FREECAD ASSEMBLY — COMPONENT RECIPES ("tripod_base")

This assembly document has 14 components, labeled P0..P13 below (a component is one placed body or linked part). 14 of them carry a construction recipe — the FreeCAD feature program that regenerates the part from scratch, quoted from this document or its linked companion documents; the rest are supplied as boundary geometry only. No exploded tour is included for this assembly.
NOTE — document 2 of 2 of this assembly tour. The two overview renders and the header above are repeated from document 1; the component sections below continue where the previous document stopped.
COMPONENT P9 — recipe-attached ("Plate", modeled in this document).
Construction recipe (the document's own serialized feature program — sketch geometry with constraints, then the solid features built on it; lengths are millimeters unless a unit is written):

FEATURE [PartDesign::SubShapeBinder] Binder
  BindCopyOnChange = 0
  BindMode = 0
  ClaimChildren = false
  Context = -> Part012 [Body017.Binder.]
  Fuse = false
  MakeFace = true
  OffsetFill = false
  OffsetIntersection = false
  OffsetJoinType = 0
  OffsetOpenResult = false
  PartialLoad = false
  Relative = true
  Support = -> [Part005[Body007.]]
  _Version = 2
FEATURE [Sketcher::SketchObject] Sketch060
  ArcFitTolerance = 1e-06
  AttachmentSupport = -> [Binder]
  ExternalGeometry = -> [Binder]
  FullyConstrained = false
  MakeInternals = false
  MapMode = 5
  Placement = pos=(0,0,11) rot=(1,0,0;3.14159rad)
  sketch-geometry (30):
    g0: LineSegment [constr] StartX=-65.0269 StartY=11.2868 StartZ=0 EndX=-11.2868 EndY=65.0269 EndZ=0
    g1: LineSegment [constr] StartX=-11.2868 StartY=65.0269 StartZ=0 EndX=27.9576 EndY=25.7825 EndZ=0
    g2: LineSegment [constr] StartX=27.9576 StartY=25.7825 StartZ=0 EndX=-25.7825 EndY=-27.9576 EndZ=0
    g3: LineSegment [constr] StartX=-25.7825 StartY=-27.9576 StartZ=0 EndX=-65.0269 EndY=11.2868 EndZ=0
    g4: LineSegment [constr] StartX=-38.1569 StartY=38.1569 StartZ=0 EndX=1.08757 EndY=-1.08757 EndZ=0
    g5: Circle CenterX=-65.0269 CenterY=11.2868 CenterZ=0 NormalX=0 NormalY=0 NormalZ=1 AngleXU=0 Radius=1.25
    g6: Circle CenterX=-25.7825 CenterY=-27.9576 CenterZ=0 NormalX=0 NormalY=0 NormalZ=1 AngleXU=0 Radius=1.25
    g7: Circle CenterX=27.9576 CenterY=25.7825 CenterZ=0 NormalX=0 NormalY=0 NormalZ=1 AngleXU=0 Radius=1.25
    g8: Circle CenterX=-11.2868 CenterY=65.0269 CenterZ=0 NormalX=0 NormalY=0 NormalZ=1 AngleXU=0 Radius=1.25
    g9: Circle CenterX=-36.7426 CenterY=39.5711 CenterZ=0 NormalX=0 NormalY=0 NormalZ=1 AngleXU=0 Radius=1.25
    g10: Circle CenterX=-39.5711 CenterY=36.7426 CenterZ=0 NormalX=0 NormalY=0 NormalZ=1 AngleXU=0 Radius=1.25
    g11: Circle CenterX=-0.326641 CenterY=-2.50179 CenterZ=0 NormalX=0 NormalY=0 NormalZ=1 AngleXU=0 Radius=1.25
    g12: Circle CenterX=2.50179 CenterY=0.326641 CenterZ=0 NormalX=0 NormalY=0 NormalZ=1 AngleXU=0 Radius=1.25
    g13: GeomPoint [constr] X=-18.5346 Y=18.5346 Z=0
    g14: LineSegment [constr] StartX=0 StartY=65 StartZ=0 EndX=-65 EndY=0 EndZ=0
    g15: GeomPoint [constr] X=-32.5 Y=32.5 Z=0
    g16: LineSegment StartX=-68.5624 StartY=14.8223 StartZ=0 EndX=-14.8223 EndY=68.5624 EndZ=0
    g17: LineSegment StartX=30.079 StartY=23.6612 StartZ=0 EndX=-23.6612 EndY=-30.079 EndZ=0
    g18: ArcOfCircle CenterX=-11.2868 CenterY=65.0269 CenterZ=0 NormalX=0 NormalY=0 NormalZ=1 AngleXU=0 Radius=5 StartAngle=1.56841 EndAngle=2.35619
    g19: ArcOfCircle CenterX=0 CenterY=65 CenterZ=0 NormalX=0 NormalY=0 NormalZ=1 AngleXU=0 Radius=5 StartAngle=0.577784 EndAngle=1.56841
    g20: LineSegment StartX=-11.2749 StartY=70.0269 StartZ=0 EndX=0.0119218 EndY=70 EndZ=0
    g21: ArcOfCircle CenterX=27.9576 CenterY=25.7825 CenterZ=0 NormalX=0 NormalY=0 NormalZ=1 AngleXU=0 Radius=3 StartAngle=5.49779 EndAngle=6.86097
    g22: LineSegment StartX=4.18837 StartY=67.7308 StartZ=0 EndX=30.4707 EndY=27.421 EndZ=0
    g23: ArcOfCircle CenterX=-25.7825 CenterY=-27.9576 CenterZ=0 NormalX=0 NormalY=0 NormalZ=1 AngleXU=0 Radius=3 StartAngle=4.1346 EndAngle=5.49779
    g24: ArcOfCircle CenterX=-65.0269 CenterY=11.2868 CenterZ=0 NormalX=0 NormalY=0 NormalZ=1 AngleXU=0 Radius=5 StartAngle=2.35619 EndAngle=3.14398
    g25: ArcOfCircle CenterX=-65 CenterY=0 CenterZ=0 NormalX=0 NormalY=0 NormalZ=1 AngleXU=0 Radius=5 StartAngle=3.14398 EndAngle=4.1346
    g26: LineSegment StartX=-70.0269 StartY=11.2749 StartZ=0 EndX=-70 EndY=-0.0119218 EndZ=0
    g27: LineSegment StartX=-67.7308 StartY=-4.18837 StartZ=0 EndX=-27.421 EndY=-30.4707 EndZ=0
    g28: Circle CenterX=0 CenterY=65 CenterZ=0 NormalX=0 NormalY=0 NormalZ=1 AngleXU=0 Radius=1.65
    g29: Circle CenterX=-65 CenterY=0 CenterZ=0 NormalX=0 NormalY=0 NormalZ=1 AngleXU=0 Radius=1.65
  constraints (74):
    c: Coincident(g0,g1)
    c: Coincident(g1,g2)
    c: Coincident(g2,g3)
    c: Coincident(g3,g0)
    c: Angle(g3,g0) = 1.5708
    c: Angle(g0,g1) = 1.5708
    c: Equal(g1,g3)
    c: Symmetric(g0,g0,g4)
    c: Symmetric(g2,g2,g4)
    c: Distance(g0,g0) = 76
    c: Coincident(g5,g0)
    c: Coincident(g6,g2)
    c: Coincident(g7,g1)
    c: Coincident(g8,g0)
    c: PointOnObject(g9,g0)
    c: PointOnObject(g11,g2)
    c: Symmetric(g9,g10,g4)
    c: Symmetric(g12,g11,g4)
    c: Equal(g8,g9)
    c: Equal(g10,g5)
    c: Equal(g6,g11)
    c: Equal(g12,g7)
    c: Equal(g7,g8)
    c: Equal(g6,g5)
    c: Equal(g8,g5)
    c: Diameter(g8) = 2.5
    c: Distance(g10,g9) = 4
    c: Distance(g12,g11) = 4
    c: Distance(g1,g1) = 55.5
    c: Symmetric(g4,g4,g13)
    c: Parallel(g0,g14)
    c: Symmetric(g14,g14,g15)
    c: PointOnObject(g15,g4)
    c: Coincident(g14,g-4)
    c: Coincident(g14,g-3)
    c: Distance(g15,g4) = 8
    c: Coincident(g18,g0)
    c: Coincident(g18,g16)
    c: Angle(g16,g18,g16) = 3.14159
    c: Coincident(g19,g14)
    c: Coincident(g20,g18)
    c: Coincident(g20,g19)
    c: Angle(g20,g18,g18) = 3.14159
    c: Angle(g19,g20,g19) = 3.14159
    c: Radius(g19) = 5
    c: Radius(g18) = 5
    c: Coincident(g21,g1)
    c: Coincident(g17,g21)
    c: Angle(g17,g21,g17) = 3.14159
    c: Coincident(g22,g19)
    c: Coincident(g22,g21)
    c: Angle(g21,g22,g21) = 3.14159
    c: Radius(g21) = 3
    c: Coincident(g23,g2)
    c: Coincident(g17,g23)
    c: Angle(g17,g23,g17) = 3.14159
    c: Coincident(g24,g0)
    c: Coincident(g25,g14)
    c: Coincident(g16,g24)
    c: Angle(g16,g24,g16) = 3.14159
    c: Coincident(g26,g24)
    c: Coincident(g26,g25)
    c: Angle(g25,g26,g25) = 0
    c: Equal(g24,g25)
    c: Equal(g24,g18)
    c: Angle(g26,g24,g24) = 0
    c: Coincident(g27,g25)
    c: Coincident(g27,g23)
    c: Angle(g23,g27,g23) = 0
    c: Angle(g27,g25,g25) = 0
    c: Equal(g21,g23)
    c: Angle(g22,g19,g19) = 3.14159
    c: Coincident(g28,g14)
    c: Coincident(g29,g14)
FEATURE [PartDesign::Pad] Pad017
  Direction = (0,0,-1)
  Length = 5
  Length2 = 10
  Profile = -> Sketch060
  ReferenceAxis = -> Sketch060 [N_Axis]
  Suppressed = false
  Type = 0
FEATURE [Sketcher::SketchObject] Sketch061
  ArcFitTolerance = 1e-06
  AttachmentSupport = -> [Pad017]
  ExternalGeometry = -> [Pad017]
  FullyConstrained = false
  MakeInternals = false
  MapMode = 5
  Placement = pos=(0,0,11) rot=(0,0,1;0rad)
  sketch-geometry (4):
    g0: Circle CenterX=-65 CenterY=0 CenterZ=0 NormalX=0 NormalY=0 NormalZ=1 AngleXU=0 Radius=3.25
    g1: Circle CenterX=0 CenterY=-65 CenterZ=0 NormalX=0 NormalY=0 NormalZ=1 AngleXU=0 Radius=3.25
    g2: Circle CenterX=0 CenterY=-65 CenterZ=0 NormalX=0 NormalY=0 NormalZ=1 AngleXU=0 Radius=1.65
    g3: Circle CenterX=-65 CenterY=0 CenterZ=0 NormalX=0 NormalY=0 NormalZ=1 AngleXU=0 Radius=1.65
  constraints (6):
    c: Coincident(g0,g-4)
    c: Coincident(g1,g-3)
    c: Equal(g0,g1)
    c: Diameter(g1) = 6.5
    c: Coincident(g2,g1)
    c: Coincident(g3,g0)
FEATURE [PartDesign::Pad] Pad018
  BaseFeature = -> Pad017
  Direction = (0,0,1)
  Length = 2
  Length2 = 10
  Profile = -> Sketch061
  ReferenceAxis = -> Sketch061 [N_Axis]
  Suppressed = false
  Type = 0
FEATURE [PartDesign::Fillet] Fillet004
  Base = -> Pad018 [Edge23,Edge26]
  BaseFeature = -> Pad018
  Radius = 1
  SupportTransform = false
  Suppressed = false
  UseAllEdges = false
FEATURE [Sketcher::SketchObject] Sketch062
  ArcFitTolerance = 1e-06
  AttachmentSupport = -> [Fillet004]
  ExternalGeometry = -> [Fillet004]
  FullyConstrained = false
  MakeInternals = false
  MapMode = 5
  Placement = pos=(0,0,11) rot=(0,0,1;0rad)
  sketch-geometry (56):
    g0: LineSegment StartX=-63.0269 StartY=-12.4415 StartZ=0 EndX=-63.0269 EndY=-10.1321 EndZ=0
    g1: LineSegment StartX=-63.0269 StartY=-10.1321 StartZ=0 EndX=-65.0269 EndY=-8.9774 EndZ=0
    g2: LineSegment StartX=-65.0269 StartY=-8.9774 StartZ=0 EndX=-67.0269 EndY=-10.1321 EndZ=0
    g3: LineSegment StartX=-67.0269 StartY=-10.1321 StartZ=0 EndX=-67.0269 EndY=-12.4415 EndZ=0
    g4: LineSegment StartX=-67.0269 StartY=-12.4415 StartZ=0 EndX=-65.0269 EndY=-13.5962 EndZ=0
    g5: LineSegment StartX=-65.0269 StartY=-13.5962 StartZ=0 EndX=-63.0269 EndY=-12.4415 EndZ=0
    g6: Circle [constr] CenterX=-65.0269 CenterY=-11.2868 CenterZ=0 NormalX=0 NormalY=0 NormalZ=1 AngleXU=0 Radius=2.3094
    g7: LineSegment StartX=-41.8018 StartY=-36.1449 StartZ=0 EndX=-41.2041 EndY=-38.3756 EndZ=0
    g8: LineSegment StartX=-41.2041 StartY=-38.3756 StartZ=0 EndX=-38.9734 EndY=-38.9734 EndZ=0
    g9: LineSegment StartX=-38.9734 StartY=-38.9734 StartZ=0 EndX=-37.3404 EndY=-37.3404 EndZ=0
    g10: LineSegment StartX=-37.3404 StartY=-37.3404 StartZ=0 EndX=-37.9381 EndY=-35.1096 EndZ=0
    g11: LineSegment StartX=-37.9381 StartY=-35.1096 StartZ=0 EndX=-40.1688 EndY=-34.5119 EndZ=0
    g12: LineSegment StartX=-40.1688 StartY=-34.5119 StartZ=0 EndX=-41.8018 EndY=-36.1449 EndZ=0
    g13: Circle [constr] CenterX=-39.5711 CenterY=-36.7426 CenterZ=0 NormalX=0 NormalY=0 NormalZ=1 AngleXU=0 Radius=2.3094
    g14: LineSegment StartX=-35.1096 StartY=-37.9381 StartZ=0 EndX=-37.3404 EndY=-37.3404 EndZ=0
    g15: LineSegment StartX=-37.3404 StartY=-37.3404 StartZ=0 EndX=-38.9734 EndY=-38.9734 EndZ=0
    g16: LineSegment StartX=-38.9734 StartY=-38.9734 StartZ=0 EndX=-38.3756 EndY=-41.2041 EndZ=0
    g17: LineSegment StartX=-38.3756 StartY=-41.2041 StartZ=0 EndX=-36.1449 EndY=-41.8018 EndZ=0
    g18: LineSegment StartX=-36.1449 StartY=-41.8018 StartZ=0 EndX=-34.5119 EndY=-40.1688 EndZ=0
    g19: LineSegment StartX=-34.5119 StartY=-40.1688 StartZ=0 EndX=-35.1096 EndY=-37.9381 EndZ=0
    g20: Circle [constr] CenterX=-36.7426 CenterY=-39.5711 CenterZ=0 NormalX=0 NormalY=0 NormalZ=1 AngleXU=0 Radius=2.3094
    g21: LineSegment StartX=-11.2868 StartY=-62.7175 StartZ=0 EndX=-13.2868 EndY=-63.8722 EndZ=0
    g22: LineSegment StartX=-13.2868 StartY=-63.8722 StartZ=0 EndX=-13.2868 EndY=-66.1816 EndZ=0
    g23: LineSegment StartX=-13.2868 StartY=-66.1816 StartZ=0 EndX=-11.2868 EndY=-67.3363 EndZ=0
    g24: LineSegment StartX=-11.2868 StartY=-67.3363 StartZ=0 EndX=-9.2868 EndY=-66.1816 EndZ=0
    g25: LineSegment StartX=-9.2868 StartY=-66.1816 StartZ=0 EndX=-9.2868 EndY=-63.8722 EndZ=0
    g26: LineSegment StartX=-9.2868 StartY=-63.8722 StartZ=0 EndX=-11.2868 EndY=-62.7175 EndZ=0
    g27: Circle [constr] CenterX=-11.2868 CenterY=-65.0269 CenterZ=0 NormalX=0 NormalY=0 NormalZ=1 AngleXU=0 Radius=2.3094
    g28: LineSegment StartX=29.1123 StartY=-23.7825 StartZ=0 EndX=26.8029 EndY=-23.7825 EndZ=0
    g29: LineSegment StartX=26.8029 StartY=-23.7825 StartZ=0 EndX=25.6482 EndY=-25.7825 EndZ=0
    g30: LineSegment StartX=25.6482 StartY=-25.7825 StartZ=0 EndX=26.8029 EndY=-27.7825 EndZ=0
    g31: LineSegment StartX=26.8029 StartY=-27.7825 StartZ=0 EndX=29.1123 EndY=-27.7825 EndZ=0
    g32: LineSegment StartX=29.1123 StartY=-27.7825 StartZ=0 EndX=30.267 EndY=-25.7825 EndZ=0
    g33: LineSegment StartX=30.267 StartY=-25.7825 StartZ=0 EndX=29.1123 EndY=-23.7825 EndZ=0
    g34: Circle [constr] CenterX=27.9576 CenterY=-25.7825 CenterZ=0 NormalX=0 NormalY=0 NormalZ=1 AngleXU=0 Radius=2.3094
    g35: LineSegment StartX=4.7325 StartY=-0.924358 StartZ=0 EndX=4.13478 EndY=1.30635 EndZ=0
    g36: LineSegment StartX=4.13478 StartY=1.30635 StartZ=0 EndX=1.90407 EndY=1.90407 EndZ=0
    g37: LineSegment StartX=1.90407 StartY=1.90407 StartZ=0 EndX=0.271076 EndY=0.271076 EndZ=0
    g38: LineSegment StartX=0.271076 StartY=0.271076 StartZ=0 EndX=0.868793 EndY=-1.95963 EndZ=0
    g39: LineSegment StartX=0.868793 StartY=-1.95963 StartZ=0 EndX=3.0995 EndY=-2.55735 EndZ=0
    g40: LineSegment StartX=3.0995 StartY=-2.55735 StartZ=0 EndX=4.7325 EndY=-0.924358 EndZ=0
    g41: Circle [constr] CenterX=2.50179 CenterY=-0.326641 CenterZ=0 NormalX=0 NormalY=0 NormalZ=1 AngleXU=0 Radius=2.3094
    g42: LineSegment StartX=-2.55735 StartY=3.0995 StartZ=0 EndX=-1.95963 EndY=0.868793 EndZ=0
    g43: LineSegment StartX=-1.95963 StartY=0.868793 StartZ=0 EndX=0.271076 EndY=0.271076 EndZ=0
    g44: LineSegment StartX=0.271076 StartY=0.271076 StartZ=0 EndX=1.90407 EndY=1.90407 EndZ=0
    g45: LineSegment StartX=1.90407 StartY=1.90407 StartZ=0 EndX=1.30635 EndY=4.13478 EndZ=0
    g46: LineSegment StartX=1.30635 StartY=4.13478 StartZ=0 EndX=-0.924358 EndY=4.7325 EndZ=0
    g47: LineSegment StartX=-0.924358 StartY=4.7325 StartZ=0 EndX=-2.55735 EndY=3.0995 EndZ=0
    g48: Circle [constr] CenterX=-0.326641 CenterY=2.50179 CenterZ=0 NormalX=0 NormalY=0 NormalZ=1 AngleXU=0 Radius=2.3094
    g49: LineSegment StartX=-26.1927 StartY=30.2303 StartZ=0 EndX=-27.9558 EndY=28.7387 EndZ=0
    g50: LineSegment StartX=-27.9558 StartY=28.7387 StartZ=0 EndX=-27.5456 EndY=26.466 EndZ=0
    g51: LineSegment StartX=-27.5456 StartY=26.466 StartZ=0 EndX=-25.3722 EndY=25.685 EndZ=0
    g52: LineSegment StartX=-25.3722 StartY=25.685 StartZ=0 EndX=-23.6092 EndY=27.1766 EndZ=0
    g53: LineSegment StartX=-23.6092 StartY=27.1766 StartZ=0 EndX=-24.0194 EndY=29.4492 EndZ=0
    g54: LineSegment StartX=-24.0194 StartY=29.4492 StartZ=0 EndX=-26.1927 EndY=30.2303 EndZ=0
    g55: Circle [constr] CenterX=-25.7825 CenterY=27.9576 CenterZ=0 NormalX=0 NormalY=0 NormalZ=1 AngleXU=0 Radius=2.3094
  constraints (125):
    c: Coincident(g0,g1)
    c: Coincident(g1,g2)
    c: Coincident(g2,g3)
    c: Coincident(g3,g4)
    c: Coincident(g4,g5)
    c: Coincident(g5,g0)
    c: Equal(g0, g1-g5) x5
    c: PointOnObject(g0,g6)
    c: PointOnObject(g1,g6)
    c: PointOnObject(g2,g6)
    c: PointOnObject(g3,g6)
    c: PointOnObject(g4,g6)
    c: PointOnObject(g5,g6)
    c: Coincident(g6,g-4)
    c: Coincident(g7,g8)
    c: Coincident(g8,g9)
    c: Coincident(g9,g10)
    c: Coincident(g10,g11)
    c: Coincident(g11,g12)
    c: Coincident(g12,g7)
    c: Equal(g7, g8-g12) x5
    c: PointOnObject(g7,g13)
    c: PointOnObject(g8,g13)
    c: PointOnObject(g9,g13)
    c: PointOnObject(g10,g13)
    c: PointOnObject(g11,g13)
    c: PointOnObject(g12,g13)
    c: Coincident(g13,g-8)
    c: Coincident(g14,g15)
    c: Coincident(g15,g16)
    c: Coincident(g16,g17)
    c: Coincident(g17,g18)
    c: Coincident(g18,g19)
    c: Coincident(g19,g14)
    c: Equal(g14, g15-g19) x5
    c: PointOnObject(g14,g20)
    c: PointOnObject(g15,g20)
    c: PointOnObject(g16,g20)
    c: PointOnObject(g17,g20)
    c: PointOnObject(g18,g20)
    c: PointOnObject(g19,g20)
    c: Coincident(g20,g-9)
    c: Coincident(g21,g22)
    c: Coincident(g22,g23)
    c: Coincident(g23,g24)
    c: Coincident(g24,g25)
    c: Coincident(g25,g26)
    c: Coincident(g26,g21)
    c: Equal(g21, g22-g26) x5
    c: PointOnObject(g21,g27)
    c: PointOnObject(g22,g27)
    c: PointOnObject(g23,g27)
    c: PointOnObject(g24,g27)
    c: PointOnObject(g25,g27)
    c: PointOnObject(g26,g27)
    c: Coincident(g27,g-10)
    c: Coincident(g28,g29)
    c: Coincident(g29,g30)
    c: Coincident(g30,g31)
    c: Coincident(g31,g32)
    c: Coincident(g32,g33)
    c: Coincident(g33,g28)
    c: Equal(g28, g29-g33) x5
    c: PointOnObject(g28,g34)
    c: PointOnObject(g29,g34)
    c: PointOnObject(g30,g34)
    c: PointOnObject(g31,g34)
    c: PointOnObject(g32,g34)
    c: PointOnObject(g33,g34)
    c: Coincident(g34,g-7)
    c: Coincident(g35,g36)
    c: Coincident(g36,g37)
    c: Coincident(g37,g38)
    c: Coincident(g38,g39)
    c: Coincident(g39,g40)
    c: Coincident(g40,g35)
    c: Equal(g35, g36-g40) x5
    c: PointOnObject(g35,g41)
    c: PointOnObject(g36,g41)
    c: PointOnObject(g37,g41)
    c: PointOnObject(g38,g41)
    c: PointOnObject(g39,g41)
    c: PointOnObject(g40,g41)
    c: Coincident(g41,g-6)
    c: Coincident(g42,g43)
    c: Coincident(g43,g44)
    c: Coincident(g44,g45)
    c: Coincident(g45,g46)
    c: Coincident(g46,g47)
    c: Coincident(g47,g42)
    c: Equal(g42, g43-g47) x5
    c: PointOnObject(g42,g48)
    c: PointOnObject(g43,g48)
    c: PointOnObject(g44,g48)
    c: PointOnObject(g45,g48)
    c: PointOnObject(g46,g48)
    c: PointOnObject(g47,g48)
    c: Coincident(g48,g-5)
    c: Coincident(g49,g50)
    c: Coincident(g50,g51)
    c: Coincident(g51,g52)
    c: Coincident(g52,g53)
    c: Coincident(g53,g54)
    c: Coincident(g54,g49)
    c: Equal(g49, g50-g54) x5
    c: PointOnObject(g49,g55)
    c: PointOnObject(g50,g55)
    c: PointOnObject(g51,g55)
    c: PointOnObject(g52,g55)
    c: PointOnObject(g53,g55)
    c: PointOnObject(g54,g55)
    c: Coincident(g55,g-3)
    c: Equal(g55,g48)
    c: Equal(g48,g41)
    c: Equal(g41,g34)
    c: Equal(g34,g27)
    c: Equal(g27,g20)
    c: Equal(g20,g13)
    c: Equal(g13,g6)
    c: Vertical(g0)
    c: DistanceX(g2,g0) = 4
    c: Coincident(g36,g44)
    c: Coincident(g14,g9)
    c: Horizontal(g28)
    c: Vertical(g25)
FEATURE [PartDesign::Pocket] Pocket042
  BaseFeature = -> Fillet004
  Direction = (0,0,-1)
  Length = 2
  Length2 = 5
  Profile = -> Sketch062
  ReferenceAxis = -> Sketch062 [N_Axis]
  Suppressed = false
  Type = 0
FEATURE [Sketcher::SketchObject] Sketch063
  ArcFitTolerance = 1e-06
  AttachmentSupport = -> [Pocket042]
  ExternalGeometry = -> [Pocket042]
  FullyConstrained = true
  MakeInternals = false
  MapMode = 5
  Placement = pos=(0,0,6) rot=(1,0,0;3.14159rad)
  sketch-geometry (8):
    g0: LineSegment StartX=-25.3204 StartY=-24.9934 StartZ=0 EndX=24.9934 EndY=25.3204 EndZ=0
    g1: LineSegment StartX=24.9934 StartY=25.3204 StartZ=0 EndX=-11.7489 EndY=62.0627 EndZ=0
    g2: LineSegment StartX=-11.7489 StartY=62.0627 StartZ=0 EndX=-62.0627 EndY=11.7489 EndZ=0
    g3: LineSegment StartX=-62.0627 StartY=11.7489 StartZ=0 EndX=-25.3204 EndY=-24.9934 EndZ=0
    g4: LineSegment [constr] StartX=-62.0627 StartY=11.7489 StartZ=0 EndX=24.9934 EndY=25.3204 EndZ=0
    g5: LineSegment [constr] StartX=-25.3204 StartY=-24.9934 StartZ=0 EndX=-11.7489 EndY=62.0627 EndZ=0
    g6: GeomPoint [constr] X=-18.5346 Y=18.5346 Z=0
    g7: GeomPoint [constr] X=-18.5346 Y=18.5346 Z=0
  constraints (16):
    c: Coincident(g0,g1)
    c: Coincident(g1,g2)
    c: Coincident(g2,g3)
    c: Coincident(g3,g0)
    c: Coincident(g4,g2)
    c: Coincident(g4,g0)
    c: Coincident(g5,g0)
    c: Coincident(g5,g1)
    c: Symmetric(g4,g4,g6)
    c: Symmetric(g5,g5,g7)
    c: Coincident(g7,g6)
    c: Angle(g2,g3,g2) = 1.5708
    c: PointOnObject(g-3,g4)
    c: Symmetric(g-3,g-5,g6)
    c: PointOnObject(g-4,g5)
    c: Distance(g-5,g0) = 3
FEATURE [PartDesign::Pocket] Pocket043
  BaseFeature = -> Pocket042
  Direction = (0,0,1)
  Length = 5
  Length2 = 5
  Profile = -> Sketch063
  ReferenceAxis = -> Sketch063 [N_Axis]
  Suppressed = false
  Type = 1
FEATURE [Sketcher::SketchObject] Sketch076
  ArcFitTolerance = 1e-06
  AttachmentSupport = -> [Pocket043]
  ExternalGeometry = -> [Pocket043]
  FullyConstrained = true
  MakeInternals = false
  MapMode = 5
  Placement = pos=(0,0,11) rot=(0,0,1;0rad)
  sketch-geometry (5):
    g0: LineSegment StartX=-3.86218 StartY=10.28 StartZ=0 EndX=10.28 EndY=-3.86218 EndZ=0
    g1: LineSegment StartX=10.28 StartY=-3.86218 StartZ=0 EndX=15.5833 EndY=1.44113 EndZ=0
    g2: LineSegment StartX=15.5833 StartY=1.44113 StartZ=0 EndX=1.44113 EndY=15.5833 EndZ=0
    g3: LineSegment StartX=1.44113 StartY=15.5833 StartZ=0 EndX=-3.86218 EndY=10.28 EndZ=0
    g4: LineSegment [constr] StartX=3.20889 StartY=3.20889 StartZ=0 EndX=8.51219 EndY=8.51219 EndZ=0
  constraints (14):
    c: PointOnObject(g0,g-3)
    c: PointOnObject(g0,g-3)
    c: Coincident(g0,g1)
    c: Coincident(g1,g2)
    c: Coincident(g2,g3)
    c: Coincident(g3,g0)
    c: Parallel(g1,g3)
    c: Symmetric(g0,g0,g4)
    c: Symmetric(g2,g2,g4)
    c: PointOnObject(g-1,g4)
    c: Distance(g0,g0) = 20
    c: Parallel(g2,g0)
    c: Angle(g1,g0) = 1.5708
    c: Distance(g1,g1) = 7.5
FEATURE [PartDesign::Pad] Pad025
  BaseFeature = -> Pocket043
  Direction = (0,0,1)
  Length = 60
  Length2 = 10
  Profile = -> Sketch076
  ReferenceAxis = -> Sketch076 [N_Axis]
  Reversed = true
  Suppressed = false
  Type = 0
FEATURE [Sketcher::SketchObject] Sketch082
  ArcFitTolerance = 1e-06
  AttachmentSupport = -> [Pad025]
  ExternalGeometry = -> [Pad025]
  FullyConstrained = true
  MakeInternals = false
  MapMode = 5
  Placement = pos=(0,0,-49) rot=(1,0,0;3.14159rad)
  sketch-geometry (7):
    g0: LineSegment StartX=-3.86218 StartY=-10.28 StartZ=0 EndX=10.28 EndY=3.86218 EndZ=0
    g1: LineSegment StartX=10.28 StartY=3.86218 StartZ=0 EndX=2.12132 EndY=12.0208 EndZ=0
    g2: LineSegment StartX=2.12132 StartY=12.0208 StartZ=0 EndX=-12.0208 EndY=-2.12132 EndZ=0
    g3: LineSegment StartX=-12.0208 StartY=-2.12132 StartZ=0 EndX=-3.86218 EndY=-10.28 EndZ=0
    g4: Circle [constr] CenterX=0 CenterY=0 CenterZ=0 NormalX=0 NormalY=0 NormalZ=1 AngleXU=0 Radius=5
    g5: GeomPoint [constr] X=-3.53553 Y=3.53553 Z=0
    g6: LineSegment [constr] StartX=-4.94975 StartY=4.94975 StartZ=0 EndX=0 EndY=0 EndZ=0
  constraints (16):
    c: Coincident(g-5,g0)
    c: Coincident(g0,g-4)
    c: Coincident(g0,g1)
    c: Coincident(g1,g2)
    c: Coincident(g2,g3)
    c: Coincident(g3,g0)
    c: Parallel(g1,g-4)
    c: Parallel(g0,g2)
    c: Equal(g2,g0)
    c: Coincident(g4,g-1)
    c: Diameter(g4) = 10
    c: PointOnObject(g5,g4)
    c: Symmetric(g2,g2,g6)
    c: Coincident(g6,g4)
    c: PointOnObject(g5,g6)
    c: Distance(g5,g6) = 2
FEATURE [PartDesign::Pad] Pad026
  BaseFeature = -> Pad025
  Direction = (0,0,-1)
  Length = 14.5
  Length2 = 10
  Profile = -> Sketch082
  ReferenceAxis = -> Sketch082 [N_Axis]
  Reversed = true
  Suppressed = false
  Type = 0
FEATURE [Sketcher::SketchObject] Sketch083
  ArcFitTolerance = 1e-06
  AttachmentSupport = -> [Pad026]
  FullyConstrained = true
  MakeInternals = false
  MapMode = 5
  Placement = pos=(0,0,-49) rot=(1,0,0;3.14159rad)
  sketch-geometry (1):
    g0: Circle CenterX=0 CenterY=0 CenterZ=0 NormalX=0 NormalY=0 NormalZ=1 AngleXU=0 Radius=5
  constraints (2):
    c: Coincident(g0,g-1)
    c: Diameter(g0) = 10
FEATURE [PartDesign::Pocket] Pocket048
  BaseFeature = -> Pad026
  Direction = (0,0,1)
  Length = 5
  Length2 = 5
  Profile = -> Sketch083
  ReferenceAxis = -> Sketch083 [N_Axis]
  Suppressed = false
  Type = 2
FEATURE [Sketcher::SketchObject] Sketch084
  ArcFitTolerance = 1e-06
  AttachmentSupport = -> [Pocket048]
  ExternalGeometry = -> [Pocket048]
  FullyConstrained = true
  MakeInternals = false
  MapMode = 5
  Placement = pos=(-4.94975,-4.94975,0) rot=(0.862856,-0.357407,-0.357407;1.71777rad)
  sketch-geometry (8):
    g0: LineSegment StartX=-5.125 StartY=-47 StartZ=0 EndX=5.125 EndY=-47 EndZ=0
    g1: LineSegment StartX=5.125 StartY=-47 StartZ=0 EndX=7 EndY=-34.5 EndZ=0
    g2: LineSegment StartX=-7 StartY=-34.5 StartZ=0 EndX=-5.125 EndY=-47 EndZ=0
    g3: LineSegment StartX=-7 StartY=-34.5 StartZ=0 EndX=-10 EndY=-34.5 EndZ=0
    g4: LineSegment StartX=-10 StartY=-34.5 StartZ=0 EndX=-10 EndY=6 EndZ=0
    g5: LineSegment StartX=-10 StartY=6 StartZ=0 EndX=10 EndY=6 EndZ=0
    g6: LineSegment StartX=10 StartY=6 StartZ=0 EndX=10 EndY=-34.5 EndZ=0
    g7: LineSegment StartX=10 StartY=-34.5 StartZ=0 EndX=7 EndY=-34.5 EndZ=0
  constraints (19):
    c: Coincident(g0,g1)
    c: Coincident(g2,g0)
    c: Symmetric(g0,g0,g-2)
    c: Symmetric(g1,g2,g-2)
    c: DistanceY(g0,g1) = 12.5
    c: DistanceY(g-4,g0) = 2
    c: DistanceX(g0,g0) = 10.25
    c: DistanceX(g2,g1) = 14
    c: Coincident(g2,g3)
    c: Coincident(g3,g-7)
    c: Coincident(g3,g4)
    c: Coincident(g4,g5)
    c: Coincident(g5,g6)
    c: Coincident(g6,g-7)
    c: Coincident(g6,g7)
    c: Coincident(g7,g1)
    c: PointOnObject(g5,g-5)
    c: Horizontal(g5)
    c: Coincident(g4,g-6)
FEATURE [PartDesign::Pocket] Pocket049
  BaseFeature = -> Pocket048
  Direction = (0.707107,0.707107,0)
  Length = 13
  Length2 = 5
  Profile = -> Sketch084
  ReferenceAxis = -> Sketch084 [N_Axis]
  Suppressed = false
  Type = 0
FEATURE [PartDesign::Body] Body017
  AllowCompound = false
  Group = -> [Binder,Sketch060,Pad017,Sketch061,Pad018,Fillet004,Sketch062,Pocket042,Sketch063,Pocket043,Sketch076,Pad025,Sketch082,Pad026,Sketch083,Pocket048,Sketch084,Pocket049]
  Origin = -> Origin032
  Tip = -> Pocket049
COMPONENT P10 — recipe-attached ("inner", modeled in this document).
Construction recipe (the document's own serialized feature program — sketch geometry with constraints, then the solid features built on it; lengths are millimeters unless a unit is written):

FEATURE [PartDesign::SubShapeBinder] Binder003
  BindCopyOnChange = 0
  BindMode = 0
  ClaimChildren = false
  Fuse = false
  MakeFace = true
  OffsetFill = false
  OffsetIntersection = false
  OffsetJoinType = 0
  OffsetOpenResult = false
  PartialLoad = false
  Relative = true
  Support = -> [Part005[Body007.]]
  _Version = 2
FEATURE [Sketcher::SketchObject] Sketch085
  ArcFitTolerance = 1e-06
  AttachmentSupport = -> [Binder003]
  ExternalGeometry = -> [Binder003]
  FullyConstrained = false
  MakeInternals = false
  MapMode = 5
  Placement = pos=(0,0,9) rot=(1,0,0;3.14159rad)
  sketch-geometry (6):
    g0: ArcOfCircle CenterX=-65 CenterY=0 CenterZ=0 NormalX=0 NormalY=0 NormalZ=1 AngleXU=0 Radius=5 StartAngle=2.35619 EndAngle=5.49779
    g1: ArcOfCircle CenterX=0 CenterY=65 CenterZ=0 NormalX=0 NormalY=0 NormalZ=1 AngleXU=0 Radius=5 StartAngle=5.49779 EndAngle=8.63938
    g2: LineSegment StartX=-68.5355 StartY=3.53553 StartZ=0 EndX=-3.53553 EndY=68.5355 EndZ=0
    g3: LineSegment StartX=-61.4645 StartY=-3.53553 StartZ=0 EndX=3.53553 EndY=61.4645 EndZ=0
    g4: Circle CenterX=-65 CenterY=0 CenterZ=0 NormalX=0 NormalY=0 NormalZ=1 AngleXU=0 Radius=1.65
    g5: Circle CenterX=0 CenterY=65 CenterZ=0 NormalX=0 NormalY=0 NormalZ=1 AngleXU=0 Radius=1.65
  constraints (10):
    c: Tangent(g0,g2) = 1.5708
    c: Tangent(g0,g3) = -1.5708
    c: Tangent(g1,g2) = 1.5708
    c: Tangent(g1,g3) = -1.5708
    c: Equal(g0,g1)
    c: Radius(g0) = 5
    c: Coincident(g0,g-4)
    c: Coincident(g1,g-3)
    c: Coincident(g4,g0)
    c: Coincident(g5,g1)
FEATURE [PartDesign::Pad] Pad027
  Direction = (0,0,-1)
  Length = 10
  Length2 = 10
  Profile = -> Sketch085
  ReferenceAxis = -> Sketch085 [N_Axis]
  Suppressed = false
  Type = 0
FEATURE [Sketcher::SketchObject] Sketch086
  ArcFitTolerance = 1e-06
  AttachmentSupport = -> [Pad027]
  ExternalGeometry = -> [Pad027]
  FullyConstrained = true
  MakeInternals = false
  MapMode = 5
  Placement = pos=(0,0,-1) rot=(1,0,0;3.14159rad)
  sketch-geometry (17):
    g0: LineSegment StartX=-0.821861 StartY=68.0672 StartZ=0 EndX=-3.06723 EndY=65.8219 EndZ=0
    g1: LineSegment StartX=-3.06723 StartY=65.8219 StartZ=0 EndX=-2.24537 EndY=62.7546 EndZ=0
    g2: LineSegment StartX=-2.24537 StartY=62.7546 StartZ=0 EndX=0.821861 EndY=61.9328 EndZ=0
    g3: LineSegment StartX=0.821861 StartY=61.9328 StartZ=0 EndX=3.06723 EndY=64.1781 EndZ=0
    g4: LineSegment StartX=3.06723 StartY=64.1781 StartZ=0 EndX=2.24537 EndY=67.2454 EndZ=0
    g5: LineSegment StartX=2.24537 StartY=67.2454 StartZ=0 EndX=-0.821861 EndY=68.0672 EndZ=0
    g6: Circle [constr] CenterX=0 CenterY=65 CenterZ=0 NormalX=0 NormalY=0 NormalZ=1 AngleXU=0 Radius=3.17543
    g7: LineSegment StartX=-65.8219 StartY=3.06723 StartZ=0 EndX=-68.0672 EndY=0.821861 EndZ=0
    g8: LineSegment StartX=-68.0672 StartY=0.821861 StartZ=0 EndX=-67.2454 EndY=-2.24537 EndZ=0
    g9: LineSegment StartX=-67.2454 StartY=-2.24537 StartZ=0 EndX=-64.1781 EndY=-3.06723 EndZ=0
    g10: LineSegment StartX=-64.1781 StartY=-3.06723 StartZ=0 EndX=-61.9328 EndY=-0.821861 EndZ=0
    g11: LineSegment StartX=-61.9328 StartY=-0.821861 StartZ=0 EndX=-62.7546 EndY=2.24537 EndZ=0
    g12: LineSegment StartX=-62.7546 StartY=2.24537 StartZ=0 EndX=-65.8219 EndY=3.06723 EndZ=0
    g13: Circle [constr] CenterX=-65 CenterY=0 CenterZ=0 NormalX=0 NormalY=0 NormalZ=1 AngleXU=0 Radius=3.17543
    g14: LineSegment [constr] StartX=-62.7546 StartY=2.24537 StartZ=0 EndX=-2.24537 EndY=62.7546 EndZ=0
    g15: LineSegment [constr] StartX=-36.0355 StartY=36.0355 StartZ=0 EndX=-28.9645 EndY=28.9645 EndZ=0
    g16: GeomPoint [constr] X=-32.5 Y=32.5 Z=0
  constraints (37):
    c: Coincident(g0,g1)
    c: Coincident(g1,g2)
    c: Coincident(g2,g3)
    c: Coincident(g3,g4)
    c: Coincident(g4,g5)
    c: Coincident(g5,g0)
    c: Equal(g0, g1-g5) x5
    c: PointOnObject(g0,g6)
    c: PointOnObject(g1,g6)
    c: PointOnObject(g2,g6)
    c: PointOnObject(g3,g6)
    c: PointOnObject(g4,g6)
    c: PointOnObject(g5,g6)
    c: Coincident(g6,g-3)
    c: Coincident(g7,g8)
    c: Coincident(g8,g9)
    c: Coincident(g9,g10)
    c: Coincident(g10,g11)
    c: Coincident(g11,g12)
    c: Coincident(g12,g7)
    c: Equal(g7, g8-g12) x5
    c: PointOnObject(g7,g13)
    c: PointOnObject(g8,g13)
    c: PointOnObject(g9,g13)
    c: PointOnObject(g10,g13)
    c: PointOnObject(g11,g13)
    c: PointOnObject(g12,g13)
    c: Coincident(g13,g-4)
    c: Equal(g13,g6)
    c: Coincident(g14,g11)
    c: Coincident(g14,g1)
    c: Parallel(g14,g-5)
    c: Symmetric(g-5,g-5,g15)
    c: Symmetric(g-6,g-6,g15)
    c: Symmetric(g15,g15,g16)
    c: PointOnObject(g16,g14)
    c: Distance(g3,g1) = 5.5
FEATURE [PartDesign::Pocket] Pocket050
  BaseFeature = -> Pad027
  Direction = (0,0,1)
  Length = 4.5
  Length2 = 5
  Profile = -> Sketch086
  ReferenceAxis = -> Sketch086 [N_Axis]
  Suppressed = false
  Type = 0
FEATURE [Sketcher::SketchObject] Sketch087
  ArcFitTolerance = 1e-06
  AttachmentSupport = -> [Pocket050]
  ExternalGeometry = -> [Pocket050]
  FullyConstrained = true
  MakeInternals = false
  MapMode = 5
  Placement = pos=(-36.0355,-36.0355,0) rot=(0.862856,-0.357407,-0.357407;1.71777rad)
  sketch-geometry (5):
    g0: LineSegment [constr] StartX=-45.9619 StartY=4 StartZ=0 EndX=45.9619 EndY=4 EndZ=0
    g1: GeomPoint [constr] X=-30 Y=4 Z=0
    g2: GeomPoint [constr] X=30 Y=4 Z=0
    g3: Circle CenterX=-30 CenterY=4 CenterZ=0 NormalX=0 NormalY=0 NormalZ=1 AngleXU=0 Radius=1.65
    g4: Circle CenterX=30 CenterY=4 CenterZ=0 NormalX=0 NormalY=0 NormalZ=1 AngleXU=0 Radius=1.65
  constraints (9):
    c: Symmetric(g-5,g-5,g0)
    c: Symmetric(g-3,g-3,g0)
    c: PointOnObject(g1,g0)
    c: Coincident(g3,g1)
    c: Coincident(g4,g2)
    c: Symmetric(g2,g1,g-2)
    c: DistanceX(g1,g2) = 60
    c: Equal(g4,g3)
    c: Diameter(g4) = 3.3
FEATURE [PartDesign::Pocket] Pocket051
  BaseFeature = -> Pocket050
  Direction = (0.707107,0.707107,1e-16)
  Length = 5
  Length2 = 5
  Profile = -> Sketch087
  ReferenceAxis = -> Sketch087 [N_Axis]
  Suppressed = false
  Type = 1
FEATURE [Sketcher::SketchObject] Sketch088
  ArcFitTolerance = 1e-06
  AttachmentSupport = -> [Pocket051]
  ExternalGeometry = -> [Pocket051]
  FullyConstrained = true
  MakeInternals = false
  MapMode = 5
  Placement = pos=(-36.0355,-36.0355,0) rot=(0.862856,-0.357407,-0.357407;1.71777rad)
  sketch-geometry (14):
    g0: LineSegment StartX=28.3834 StartY=6.8 StartZ=0 EndX=26.7668 EndY=4 EndZ=0
    g1: LineSegment StartX=26.7668 StartY=4 StartZ=0 EndX=28.3834 EndY=1.2 EndZ=0
    g2: LineSegment StartX=28.3834 StartY=1.2 StartZ=0 EndX=31.6166 EndY=1.2 EndZ=0
    g3: LineSegment StartX=31.6166 StartY=1.2 StartZ=0 EndX=33.2332 EndY=4 EndZ=0
    g4: LineSegment StartX=33.2332 StartY=4 StartZ=0 EndX=31.6166 EndY=6.8 EndZ=0
    g5: LineSegment StartX=31.6166 StartY=6.8 StartZ=0 EndX=28.3834 EndY=6.8 EndZ=0
    g6: Circle [constr] CenterX=30 CenterY=4 CenterZ=0 NormalX=0 NormalY=0 NormalZ=1 AngleXU=0 Radius=3.23316
    g7: LineSegment StartX=-31.6166 StartY=6.8 StartZ=0 EndX=-33.2332 EndY=4 EndZ=0
    g8: LineSegment StartX=-33.2332 StartY=4 StartZ=0 EndX=-31.6166 EndY=1.2 EndZ=0
    g9: LineSegment StartX=-31.6166 StartY=1.2 StartZ=0 EndX=-28.3834 EndY=1.2 EndZ=0
    g10: LineSegment StartX=-28.3834 StartY=1.2 StartZ=0 EndX=-26.7668 EndY=4 EndZ=0
    g11: LineSegment StartX=-26.7668 StartY=4 StartZ=0 EndX=-28.3834 EndY=6.8 EndZ=0
    g12: LineSegment StartX=-28.3834 StartY=6.8 StartZ=0 EndX=-31.6166 EndY=6.8 EndZ=0
    g13: Circle [constr] CenterX=-30 CenterY=4 CenterZ=0 NormalX=0 NormalY=0 NormalZ=1 AngleXU=0 Radius=3.23316
  constraints (32):
    c: Coincident(g0,g1)
    c: Coincident(g1,g2)
    c: Coincident(g2,g3)
    c: Coincident(g3,g4)
    c: Coincident(g4,g5)
    c: Coincident(g5,g0)
    c: Equal(g0, g1-g5) x5
    c: PointOnObject(g0,g6)
    c: PointOnObject(g1,g6)
    c: PointOnObject(g2,g6)
    c: PointOnObject(g3,g6)
    c: PointOnObject(g4,g6)
    c: PointOnObject(g5,g6)
    c: Coincident(g6,g-4)
    c: Coincident(g7,g8)
    c: Coincident(g8,g9)
    c: Coincident(g9,g10)
    c: Coincident(g10,g11)
    c: Coincident(g11,g12)
    c: Coincident(g12,g7)
    c: Equal(g7, g8-g12) x5
    c: PointOnObject(g7,g13)
    c: PointOnObject(g8,g13)
    c: PointOnObject(g9,g13)
    c: PointOnObject(g10,g13)
    c: PointOnObject(g11,g13)
    c: PointOnObject(g12,g13)
    c: Coincident(g13,g-3)
    c: Horizontal(g12)
    c: Horizontal(g5)
    c: Equal(g6,g13)
    c: DistanceY(g1,g0) = 5.6
FEATURE [PartDesign::Pocket] Pocket052
  BaseFeature = -> Pocket051
  Direction = (0.707107,0.707107,1e-16)
  Length = 5.5
  Length2 = 5
  Profile = -> Sketch088
  ReferenceAxis = -> Sketch088 [N_Axis]
  Suppressed = false
  Type = 0
FEATURE [PartDesign::Body] Body021  label="balken"
  AllowCompound = false
  Group = -> [Binder003,Sketch085,Pad027,Sketch086,Pocket050,Sketch087,Pocket051,Sketch088,Pocket052]
  Origin = -> Origin038
  Tip = -> Pocket052
FEATURE [PartDesign::SubShapeBinder] Binder004
  BindCopyOnChange = 0
  BindMode = 0
  ClaimChildren = false
  Context = -> Part014 [Body022.Binder004.]
  Fuse = false
  MakeFace = true
  OffsetFill = false
  OffsetIntersection = false
  OffsetJoinType = 0
  OffsetOpenResult = false
  PartialLoad = false
  Relative = true
  Support = -> [Body021]
  _Version = 2
FEATURE [Sketcher::SketchObject] Sketch089
  ArcFitTolerance = 1e-06
  AttachmentSupport = -> [Binder004]
  ExternalGeometry = -> [Binder004]
  FullyConstrained = true
  MakeInternals = false
  MapMode = 5
  Placement = pos=(-28.9645,-28.9645,0) rot=(0.281085,0.678598,0.678598;2.59356rad)
  sketch-geometry (54):
    g0: Circle CenterX=-30 CenterY=4 CenterZ=0 NormalX=0 NormalY=0 NormalZ=1 AngleXU=0 Radius=1.65
    g1: Circle CenterX=30 CenterY=4 CenterZ=0 NormalX=0 NormalY=0 NormalZ=1 AngleXU=0 Radius=1.65
    g2: LineSegment [constr] StartX=-38 StartY=-3 StartZ=0 EndX=-38 EndY=-58.5 EndZ=0
    g3: LineSegment [constr] StartX=-38 StartY=-58.5 StartZ=0 EndX=38 EndY=-58.5 EndZ=0
    g4: LineSegment [constr] StartX=38 StartY=-58.5 StartZ=0 EndX=38 EndY=-3 EndZ=0
    g5: LineSegment [constr] StartX=38 StartY=-3 StartZ=0 EndX=-38 EndY=-3 EndZ=0
    g6: LineSegment [constr] StartX=8e-16 StartY=-3 StartZ=0 EndX=4.4e-15 EndY=-58.5 EndZ=0
    g7: Circle CenterX=-38 CenterY=-3 CenterZ=0 NormalX=0 NormalY=0 NormalZ=1 AngleXU=0 Radius=1.25
    g8: Circle CenterX=38 CenterY=-3 CenterZ=0 NormalX=0 NormalY=0 NormalZ=1 AngleXU=0 Radius=1.25
    g9: Circle CenterX=38 CenterY=-58.5 CenterZ=0 NormalX=0 NormalY=0 NormalZ=1 AngleXU=0 Radius=1.25
    g10: Circle CenterX=-38 CenterY=-58.5 CenterZ=0 NormalX=0 NormalY=0 NormalZ=1 AngleXU=0 Radius=1.25
    g11: Circle CenterX=2 CenterY=-3 CenterZ=0 NormalX=0 NormalY=0 NormalZ=1 AngleXU=0 Radius=1.25
    g12: Circle CenterX=-2 CenterY=-3 CenterZ=0 NormalX=0 NormalY=0 NormalZ=1 AngleXU=0 Radius=1.25
    g13: Circle CenterX=-2 CenterY=-58.5 CenterZ=0 NormalX=0 NormalY=0 NormalZ=1 AngleXU=0 Radius=1.25
    g14: Circle CenterX=2 CenterY=-58.5 CenterZ=0 NormalX=0 NormalY=0 NormalZ=1 AngleXU=0 Radius=1.25
    g15: LineSegment [constr] StartX=-41.5 StartY=-5 StartZ=0 EndX=41.5 EndY=-5 EndZ=0
    g16: LineSegment [constr] StartX=41.5 StartY=-5 StartZ=0 EndX=41.5 EndY=-56.5 EndZ=0
    g17: LineSegment [constr] StartX=41.5 StartY=-56.5 StartZ=0 EndX=-41.5 EndY=-56.5 EndZ=0
    g18: LineSegment [constr] StartX=-41.5 StartY=-56.5 StartZ=0 EndX=-41.5 EndY=-5 EndZ=0
    g19: LineSegment StartX=44.5 StartY=-1 StartZ=0 EndX=44.5 EndY=-64.5 EndZ=0
    g20: LineSegment [constr] StartX=44.5 StartY=-64.5 StartZ=0 EndX=-44.5 EndY=-64.5 EndZ=0
    g21: LineSegment StartX=-44.5 StartY=-64.5 StartZ=0 EndX=-44.5 EndY=-1 EndZ=0
    g22: LineSegment [constr] StartX=-41.5 StartY=-5 StartZ=0 EndX=-44.5 EndY=-1 EndZ=0
    g23: LineSegment [constr] StartX=41.5 StartY=-5 StartZ=0 EndX=44.5 EndY=-1 EndZ=0
    g24: GeomPoint [constr] X=-43 Y=-3 Z=0
    g25: GeomPoint [constr] X=2.6e-15 Y=-30.75 Z=0
    g26: LineSegment StartX=-35 StartY=9 StartZ=0 EndX=35 EndY=9 EndZ=0
    g27: LineSegment StartX=-44.5 StartY=-1 StartZ=0 EndX=-35 EndY=9 EndZ=0
    g28: LineSegment StartX=44.5 StartY=-1 StartZ=0 EndX=35 EndY=9 EndZ=0
    g29: ArcOfCircle CenterX=-2 CenterY=-3 CenterZ=0 NormalX=0 NormalY=0 NormalZ=1 AngleXU=0 Radius=3.5 StartAngle=3.74984 EndAngle=4.71239
    g30: ArcOfCircle CenterX=2 CenterY=-3 CenterZ=0 NormalX=0 NormalY=0 NormalZ=1 AngleXU=0 Radius=3.5 StartAngle=4.71239 EndAngle=5.67494
    g31: LineSegment StartX=-2 StartY=-6.5 StartZ=0 EndX=2 EndY=-6.5 EndZ=0
    g32: ArcOfCircle CenterX=-2 CenterY=-58.5 CenterZ=0 NormalX=0 NormalY=0 NormalZ=1 AngleXU=0 Radius=3.5 StartAngle=1.5708 EndAngle=2.53335
    g33: ArcOfCircle CenterX=2 CenterY=-58.5 CenterZ=0 NormalX=0 NormalY=0 NormalZ=1 AngleXU=0 Radius=3.5 StartAngle=0.608246 EndAngle=1.5708
    g34: LineSegment StartX=-2 StartY=-55 StartZ=0 EndX=2 EndY=-55 EndZ=0
    g35: ArcOfCircle CenterX=38 CenterY=-3 CenterZ=0 NormalX=0 NormalY=0 NormalZ=1 AngleXU=0 Radius=3.5 StartAngle=3.74984 EndAngle=4.71239
    g36: LineSegment StartX=4.87228 StartY=-5 StartZ=0 EndX=35.1277 EndY=-5 EndZ=0
    g37: LineSegment StartX=41.5 StartY=-6.5 StartZ=0 EndX=41.5 EndY=-55 EndZ=0
    g38: LineSegment StartX=41.5 StartY=-6.5 StartZ=0 EndX=38 EndY=-6.5 EndZ=0
    g39: ArcOfCircle CenterX=38 CenterY=-58.5 CenterZ=0 NormalX=0 NormalY=0 NormalZ=1 AngleXU=0 Radius=3.5 StartAngle=1.5708 EndAngle=2.53335
    g40: LineSegment StartX=38 StartY=-55 StartZ=0 EndX=41.5 EndY=-55 EndZ=0
    g41: LineSegment StartX=4.87228 StartY=-56.5 StartZ=0 EndX=35.1277 EndY=-56.5 EndZ=0
    g42: LineSegment StartX=-4.87228 StartY=-56.5 StartZ=0 EndX=-35.1277 EndY=-56.5 EndZ=0
    g43: LineSegment StartX=-41.5 StartY=-55 StartZ=0 EndX=-38 EndY=-55 EndZ=0
    g44: LineSegment StartX=-41.5 StartY=-55 StartZ=0 EndX=-41.5 EndY=-6.5 EndZ=0
    g45: LineSegment StartX=-41.5 StartY=-6.5 StartZ=0 EndX=-38 EndY=-6.5 EndZ=0
    g46: LineSegment StartX=-35.1277 StartY=-5 StartZ=0 EndX=-4.87228 EndY=-5 EndZ=0
    g47: ArcOfCircle CenterX=-38 CenterY=-58.5 CenterZ=0 NormalX=0 NormalY=0 NormalZ=1 AngleXU=0 Radius=3.5 StartAngle=0.608246 EndAngle=1.5708
    g48: ArcOfCircle CenterX=-38 CenterY=-3 CenterZ=0 NormalX=0 NormalY=0 NormalZ=1 AngleXU=0 Radius=3.5 StartAngle=4.71239 EndAngle=5.67494
    g49: Circle CenterX=-22.5 CenterY=-64.5 CenterZ=0 NormalX=0 NormalY=0 NormalZ=1 AngleXU=0 Radius=1.65
    g50: Circle CenterX=22.5 CenterY=-64.5 CenterZ=0 NormalX=0 NormalY=0 NormalZ=1 AngleXU=0 Radius=1.65
    g51: LineSegment StartX=-44.5 StartY=-64.5 StartZ=0 EndX=-25 EndY=-68.5 EndZ=0
    g52: LineSegment StartX=44.5 StartY=-64.5 StartZ=0 EndX=25 EndY=-68.5 EndZ=0
    g53: LineSegment StartX=25 StartY=-68.5 StartZ=0 EndX=-25 EndY=-68.5 EndZ=0
  constraints (145):
    c: Coincident(g0,g-3)
    c: Equal(g0,g-3)
    c: Coincident(g1,g-4)
    c: Equal(g1,g-4)
    c: Coincident(g2,g3)
    c: Coincident(g3,g4)
    c: Coincident(g4,g5)
    c: Coincident(g5,g2)
    c: Vertical(g2)
    c: Vertical(g4)
    c: Horizontal(g3)
    c: Horizontal(g5)
    c: DistanceX(g5,g5) = 76
    c: Symmetric(g5,g5,g6)
    c: Symmetric(g3,g3,g6)
    c: Coincident(g7,g2)
    c: Coincident(g9,g3)
    c: Coincident(g10,g2)
    c: Equal(g7,g10)
    c: Equal(g8,g9)
    c: Coincident(g8,g4)
    c: Equal(g9,g10)
    c: Diameter(g8) = 2.5
    c: DistanceY(g4,g4) = 55.5
    c: PointOnObject(g11,g5)
    c: PointOnObject(g12,g5)
    c: PointOnObject(g13,g3)
    c: PointOnObject(g14,g3)
    c: DistanceX(g11,g4) = 36
    c: DistanceX(g2,g12) = 36
    c: DistanceX(g12,g11) = 4
    c: Equal(g8,g11)
    c: Equal(g12,g7)
    c: Equal(g13,g14)
    c: Equal(g14,g9)
    c: Vertical(g14,g11)
    c: Vertical(g12,g13)
    c: Coincident(g15,g16)
    c: Vertical(g16)
    c: Coincident(g16,g17)
    c: Horizontal(g17)
    c: Coincident(g17,g18)
    c: Vertical(g18)
    c: Coincident(g15,g18)
    c: Vertical(g19)
    c: Coincident(g19,g20)
    c: Horizontal(g20)
    c: Coincident(g20,g21)
    c: Vertical(g21)
    c: Coincident(g22,g15)
    c: Coincident(g23,g15)
    c: Equal(g22,g23)
    c: DistanceY(g15,g21) = 4
    c: Distance(g21,g18) = 3
    c: Symmetric(g22,g22,g24)
    c: Horizontal(g24,g2)
    c: DistanceX(g24,g2) = 5
    c: Symmetric(g6,g6,g25)
    c: Symmetric(g15,g15,g6)
    c: Coincident(g19,g23)
    c: Coincident(g22,g21)
    c: Symmetric(g26,g26,g6)
    c: PointOnObject(g26,g-6)
    c: Coincident(g27,g21)
    c: Coincident(g27,g26)
    c: Coincident(g28,g19)
    c: Coincident(g28,g26)
    c: Horizontal(g19,g21)
    c: DistanceX(g26,g26) = 70
    c: DistanceX(g26,g-1) = 35
    c: DistanceY(g19,g26) = 10
    c: PointOnObject(g29,g15)
    c: Radius(g29) = 3.5
    c: PointOnObject(g30,g15)
    c: Equal(g30,g29)
    c: Coincident(g31,g29)
    c: Coincident(g31,g30)
    c: Horizontal(g31)
    c: DistanceY(g30,g30) = 3.5
    c: Coincident(g30,g11)
    c: Coincident(g29,g12)
    c: Coincident(g32,g13)
    c: PointOnObject(g32,g17)
    c: Coincident(g33,g14)
    c: PointOnObject(g33,g17)
    c: Coincident(g34,g32)
    c: Coincident(g33,g34)
    c: Radius(g32) = 3.5
    c: Symmetric(g33,g32,g6)
    c: Coincident(g35,g4)
    c: PointOnObject(g35,g15)
    c: Radius(g35) = 3.5
    c: Coincident(g36,g30)
    c: Coincident(g36,g35)
    c: PointOnObject(g37,g16)
    c: PointOnObject(g37,g16)
    c: Coincident(g38,g37)
    c: Horizontal(g38)
    c: Coincident(g35,g38)
    c: Vertical(g35,g4)
    c: Coincident(g39,g3)
    c: PointOnObject(g39,g17)
    c: Coincident(g40,g39)
    c: Horizontal(g40)
    c: Coincident(g37,g40)
    c: Radius(g39) = 3.5
    c: PointOnObject(g39,g4)
    c: Coincident(g41,g33)
    c: Coincident(g41,g39)
    c: Coincident(g42,g32)
    c: PointOnObject(g42,g17)
    c: PointOnObject(g43,g18)
    c: Horizontal(g43)
    c: Coincident(g44,g43)
    c: PointOnObject(g44,g18)
    c: Coincident(g45,g44)
    c: Horizontal(g45)
    c: PointOnObject(g46,g15)
    c: Coincident(g46,g29)
    c: Coincident(g47,g2)
    c: Coincident(g47,g42)
    c: Coincident(g47,g43)
    c: Coincident(g48,g2)
    c: Coincident(g48,g45)
    c: Coincident(g48,g46)
    c: Equal(g29,g48)
    c: Equal(g48,g47)
    c: PointOnObject(g43,g2)
    c: PointOnObject(g45,g2)
    c: Vertical(g29,g32)
    c: DistanceY(g19,g19) = 63.5
    c: DistanceY(g19,g3) = 6
    c: DistanceY(g3,g16) = 2
    c: PointOnObject(g49,g20)
    c: Equal(g50,g49)
    c: Symmetric(g50,g49,g6)
    c: DistanceX(g49,g50) = 45
    c: Equal(g50,g1)
    c: Coincident(g51,g20)
    c: Coincident(g52,g19)
    c: Coincident(g53,g52)
    c: Coincident(g53,g51)
    c: Symmetric(g52,g51,g-2)
    c: DistanceX(g53,g53) = 50
    c: DistanceY(g52,g50) = 4
FEATURE [PartDesign::Pad] Pad028
  Direction = (0.707107,0.707107,1e-16)
  Length = 5
  Length2 = 10
  Profile = -> Sketch089
  ReferenceAxis = -> Sketch089 [N_Axis]
  Suppressed = false
  Type = 0
FEATURE [Sketcher::SketchObject] Sketch090
  ArcFitTolerance = 1e-06
  AttachmentSupport = -> [Pad028]
  ExternalGeometry = -> [Pad028]
  FullyConstrained = true
  MakeInternals = false
  MapMode = 5
  Placement = pos=(-28.9645,-28.9645,-8.2e-15) rot=(0.862856,-0.357407,-0.357407;1.71777rad)
  sketch-geometry (56):
    g0: LineSegment StartX=-40 StartY=-1.8453 StartZ=0 EndX=-40 EndY=-4.1547 EndZ=0
    g1: LineSegment StartX=-40 StartY=-4.1547 StartZ=0 EndX=-38 EndY=-5.3094 EndZ=0
    g2: LineSegment StartX=-38 StartY=-5.3094 StartZ=0 EndX=-36 EndY=-4.1547 EndZ=0
    g3: LineSegment StartX=-36 StartY=-4.1547 StartZ=0 EndX=-36 EndY=-1.8453 EndZ=0
    g4: LineSegment StartX=-36 StartY=-1.8453 StartZ=0 EndX=-38 EndY=-0.690599 EndZ=0
    g5: LineSegment StartX=-38 StartY=-0.690599 StartZ=0 EndX=-40 EndY=-1.8453 EndZ=0
    g6: Circle [constr] CenterX=-38 CenterY=-3 CenterZ=0 NormalX=0 NormalY=0 NormalZ=1 AngleXU=0 Radius=2.3094
    g7: LineSegment StartX=-4 StartY=-4.1547 StartZ=0 EndX=-2 EndY=-5.3094 EndZ=0
    g8: LineSegment StartX=-2 StartY=-5.3094 StartZ=0 EndX=-2.11e-14 EndY=-4.1547 EndZ=0
    g9: LineSegment StartX=-2.11e-14 StartY=-4.1547 StartZ=0 EndX=-2.15e-14 EndY=-1.8453 EndZ=0
    g10: LineSegment StartX=-2.15e-14 StartY=-1.8453 StartZ=0 EndX=-2 EndY=-0.690599 EndZ=0
    g11: LineSegment StartX=-2 StartY=-0.690599 StartZ=0 EndX=-4 EndY=-1.8453 EndZ=0
    g12: LineSegment StartX=-4 StartY=-1.8453 StartZ=0 EndX=-4 EndY=-4.1547 EndZ=0
    g13: Circle [constr] CenterX=-2 CenterY=-3 CenterZ=0 NormalX=0 NormalY=0 NormalZ=1 AngleXU=0 Radius=2.3094
    g14: LineSegment StartX=4 StartY=-4.1547 StartZ=0 EndX=4 EndY=-1.8453 EndZ=0
    g15: LineSegment StartX=4 StartY=-1.8453 StartZ=0 EndX=2 EndY=-0.690599 EndZ=0
    g16: LineSegment StartX=2 StartY=-0.690599 StartZ=0 EndX=-7.1e-15 EndY=-1.8453 EndZ=0
    g17: LineSegment StartX=-7.1e-15 StartY=-1.8453 StartZ=0 EndX=-7e-15 EndY=-4.1547 EndZ=0
    g18: LineSegment StartX=-7e-15 StartY=-4.1547 StartZ=0 EndX=2 EndY=-5.3094 EndZ=0
    g19: LineSegment StartX=2 StartY=-5.3094 StartZ=0 EndX=4 EndY=-4.1547 EndZ=0
    g20: Circle [constr] CenterX=2 CenterY=-3 CenterZ=0 NormalX=0 NormalY=0 NormalZ=1 AngleXU=0 Radius=2.3094
    g21: LineSegment StartX=36 StartY=-4.1547 StartZ=0 EndX=38 EndY=-5.3094 EndZ=0
    g22: LineSegment StartX=38 StartY=-5.3094 StartZ=0 EndX=40 EndY=-4.1547 EndZ=0
    g23: LineSegment StartX=40 StartY=-4.1547 StartZ=0 EndX=40 EndY=-1.8453 EndZ=0
    g24: LineSegment StartX=40 StartY=-1.8453 StartZ=0 EndX=38 EndY=-0.690599 EndZ=0
    g25: LineSegment StartX=38 StartY=-0.690599 StartZ=0 EndX=36 EndY=-1.8453 EndZ=0
    g26: LineSegment StartX=36 StartY=-1.8453 StartZ=0 EndX=36 EndY=-4.1547 EndZ=0
    g27: Circle [constr] CenterX=38 CenterY=-3 CenterZ=0 NormalX=0 NormalY=0 NormalZ=1 AngleXU=0 Radius=2.3094
    g28: LineSegment StartX=36 StartY=-59.6547 StartZ=0 EndX=38 EndY=-60.8094 EndZ=0
    g29: LineSegment StartX=38 StartY=-60.8094 StartZ=0 EndX=40 EndY=-59.6547 EndZ=0
    g30: LineSegment StartX=40 StartY=-59.6547 StartZ=0 EndX=40 EndY=-57.3453 EndZ=0
    g31: LineSegment StartX=40 StartY=-57.3453 StartZ=0 EndX=38 EndY=-56.1906 EndZ=0
    g32: LineSegment StartX=38 StartY=-56.1906 StartZ=0 EndX=36 EndY=-57.3453 EndZ=0
    g33: LineSegment StartX=36 StartY=-57.3453 StartZ=0 EndX=36 EndY=-59.6547 EndZ=0
    g34: Circle [constr] CenterX=38 CenterY=-58.5 CenterZ=0 NormalX=0 NormalY=0 NormalZ=1 AngleXU=0 Radius=2.3094
    g35: LineSegment StartX=4 StartY=-59.6547 StartZ=0 EndX=4 EndY=-57.3453 EndZ=0
    g36: LineSegment StartX=4 StartY=-57.3453 StartZ=0 EndX=2 EndY=-56.1906 EndZ=0
    g37: LineSegment StartX=2 StartY=-56.1906 StartZ=0 EndX=-1.38e-14 EndY=-57.3453 EndZ=0
    g38: LineSegment StartX=-1.38e-14 StartY=-57.3453 StartZ=0 EndX=-1.39e-14 EndY=-59.6547 EndZ=0
    g39: LineSegment StartX=-1.39e-14 StartY=-59.6547 StartZ=0 EndX=2 EndY=-60.8094 EndZ=0
    g40: LineSegment StartX=2 StartY=-60.8094 StartZ=0 EndX=4 EndY=-59.6547 EndZ=0
    g41: Circle [constr] CenterX=2 CenterY=-58.5 CenterZ=0 NormalX=0 NormalY=0 NormalZ=1 AngleXU=0 Radius=2.3094
    g42: LineSegment StartX=-4 StartY=-59.6547 StartZ=0 EndX=-2 EndY=-60.8094 EndZ=0
    g43: LineSegment StartX=-2 StartY=-60.8094 StartZ=0 EndX=-2.18e-14 EndY=-59.6547 EndZ=0
    g44: LineSegment StartX=-2.18e-14 StartY=-59.6547 StartZ=0 EndX=-2.16e-14 EndY=-57.3453 EndZ=0
    g45: LineSegment StartX=-2.16e-14 StartY=-57.3453 StartZ=0 EndX=-2 EndY=-56.1906 EndZ=0
    g46: LineSegment StartX=-2 StartY=-56.1906 StartZ=0 EndX=-4 EndY=-57.3453 EndZ=0
    g47: LineSegment StartX=-4 StartY=-57.3453 StartZ=0 EndX=-4 EndY=-59.6547 EndZ=0
    g48: Circle [constr] CenterX=-2 CenterY=-58.5 CenterZ=0 NormalX=0 NormalY=0 NormalZ=1 AngleXU=0 Radius=2.3094
    g49: LineSegment StartX=-36 StartY=-59.6547 StartZ=0 EndX=-36 EndY=-57.3453 EndZ=0
    g50: LineSegment StartX=-36 StartY=-57.3453 StartZ=0 EndX=-38 EndY=-56.1906 EndZ=0
    g51: LineSegment StartX=-38 StartY=-56.1906 StartZ=0 EndX=-40 EndY=-57.3453 EndZ=0
    g52: LineSegment StartX=-40 StartY=-57.3453 StartZ=0 EndX=-40 EndY=-59.6547 EndZ=0
    g53: LineSegment StartX=-40 StartY=-59.6547 StartZ=0 EndX=-38 EndY=-60.8094 EndZ=0
    g54: LineSegment StartX=-38 StartY=-60.8094 StartZ=0 EndX=-36 EndY=-59.6547 EndZ=0
    g55: Circle [constr] CenterX=-38 CenterY=-58.5 CenterZ=0 NormalX=0 NormalY=0 NormalZ=1 AngleXU=0 Radius=2.3094
  constraints (128):
    c: Coincident(g0,g1)
    c: Coincident(g1,g2)
    c: Coincident(g2,g3)
    c: Coincident(g3,g4)
    c: Coincident(g4,g5)
    c: Coincident(g5,g0)
    c: Equal(g0, g1-g5) x5
    c: PointOnObject(g0,g6)
    c: PointOnObject(g1,g6)
    c: PointOnObject(g2,g6)
    c: PointOnObject(g3,g6)
    c: PointOnObject(g4,g6)
    c: PointOnObject(g5,g6)
    c: Coincident(g6,g-3)
    c: Coincident(g7,g8)
    c: Coincident(g8,g9)
    c: Coincident(g9,g10)
    c: Coincident(g10,g11)
    c: Coincident(g11,g12)
    c: Coincident(g12,g7)
    c: Equal(g7, g8-g12) x5
    c: PointOnObject(g7,g13)
    c: PointOnObject(g8,g13)
    c: PointOnObject(g9,g13)
    c: PointOnObject(g10,g13)
    c: PointOnObject(g11,g13)
    c: PointOnObject(g12,g13)
    c: Coincident(g13,g-4)
    c: Coincident(g14,g15)
    c: Coincident(g15,g16)
    c: Coincident(g16,g17)
    c: Coincident(g17,g18)
    c: Coincident(g18,g19)
    c: Coincident(g19,g14)
    c: Equal(g14, g15-g19) x5
    c: PointOnObject(g14,g20)
    c: PointOnObject(g15,g20)
    c: PointOnObject(g16,g20)
    c: PointOnObject(g17,g20)
    c: PointOnObject(g18,g20)
    c: PointOnObject(g19,g20)
    c: Coincident(g20,g-5)
    c: Coincident(g21,g22)
    c: Coincident(g22,g23)
    c: Coincident(g23,g24)
    c: Coincident(g24,g25)
    c: Coincident(g25,g26)
    c: Coincident(g26,g21)
    c: Equal(g21, g22-g26) x5
    c: PointOnObject(g21,g27)
    c: PointOnObject(g22,g27)
    c: PointOnObject(g23,g27)
    c: PointOnObject(g24,g27)
    c: PointOnObject(g25,g27)
    c: PointOnObject(g26,g27)
    c: Coincident(g27,g-6)
    c: Coincident(g28,g29)
    c: Coincident(g29,g30)
    c: Coincident(g30,g31)
    c: Coincident(g31,g32)
    c: Coincident(g32,g33)
    c: Coincident(g33,g28)
    c: Equal(g28, g29-g33) x5
    c: PointOnObject(g28,g34)
    c: PointOnObject(g29,g34)
    c: PointOnObject(g30,g34)
    c: PointOnObject(g31,g34)
    c: PointOnObject(g32,g34)
    c: PointOnObject(g33,g34)
    c: Coincident(g34,g-7)
    c: Coincident(g35,g36)
    c: Coincident(g36,g37)
    c: Coincident(g37,g38)
    c: Coincident(g38,g39)
    c: Coincident(g39,g40)
    c: Coincident(g40,g35)
    c: Equal(g35, g36-g40) x5
    c: PointOnObject(g35,g41)
    c: PointOnObject(g36,g41)
    c: PointOnObject(g37,g41)
    c: PointOnObject(g38,g41)
    c: PointOnObject(g39,g41)
    c: PointOnObject(g40,g41)
    c: Coincident(g41,g-8)
    c: Coincident(g42,g43)
    c: Coincident(g43,g44)
    c: Coincident(g44,g45)
    c: Coincident(g45,g46)
    c: Coincident(g46,g47)
    c: Coincident(g47,g42)
    c: Equal(g42, g43-g47) x5
    c: PointOnObject(g42,g48)
    c: PointOnObject(g43,g48)
    c: PointOnObject(g44,g48)
    c: PointOnObject(g45,g48)
    c: PointOnObject(g46,g48)
    c: PointOnObject(g47,g48)
    c: Coincident(g48,g-9)
    c: Coincident(g49,g50)
    c: Coincident(g50,g51)
    c: Coincident(g51,g52)
    c: Coincident(g52,g53)
    c: Coincident(g53,g54)
    c: Coincident(g54,g49)
    c: Equal(g49, g50-g54) x5
    c: PointOnObject(g49,g55)
    c: PointOnObject(g50,g55)
    c: PointOnObject(g51,g55)
    c: PointOnObject(g52,g55)
    c: PointOnObject(g53,g55)
    c: PointOnObject(g54,g55)
    c: Coincident(g55,g-10)
    c: Equal(g6,g13)
    c: Equal(g13,g20)
    c: Equal(g20,g27)
    c: Equal(g27,g34)
    c: Equal(g34,g41)
    c: Equal(g41,g48)
    c: Equal(g48,g55)
    c: Vertical(g3)
    c: DistanceX(g0,g2) = 4
    c: Vertical(g12)
    c: Vertical(g14)
    c: Vertical(g26)
    c: Vertical(g33)
    c: Vertical(g47)
    c: Vertical(g35)
    c: Vertical(g49)
FEATURE [PartDesign::Pocket] Pocket053
  BaseFeature = -> Pad028
  Direction = (0.707107,0.707107,0)
  Length = 2.5
  Length2 = 5
  Profile = -> Sketch090
  ReferenceAxis = -> Sketch090 [N_Axis]
  Suppressed = false
  Type = 0
FEATURE [Sketcher::SketchObject] Sketch091
  ArcFitTolerance = 1e-06
  AttachmentSupport = -> [Pocket053]
  ExternalGeometry = -> [Pocket053]
  FullyConstrained = true
  MakeInternals = false
  MapMode = 5
  Placement = pos=(-28.9645,-28.9645,-8.2e-15) rot=(0.862856,-0.357407,-0.357407;1.71777rad)
  sketch-geometry (14):
    g0: LineSegment StartX=-20.9123 StartY=-61.75 StartZ=0 EndX=-24.0877 EndY=-61.75 EndZ=0
    g1: LineSegment StartX=-24.0877 StartY=-61.75 StartZ=0 EndX=-25.6754 EndY=-64.5 EndZ=0
    g2: LineSegment StartX=-25.6754 StartY=-64.5 StartZ=0 EndX=-24.0877 EndY=-67.25 EndZ=0
    g3: LineSegment StartX=-24.0877 StartY=-67.25 StartZ=0 EndX=-20.9123 EndY=-67.25 EndZ=0
    g4: LineSegment StartX=-20.9123 StartY=-67.25 StartZ=0 EndX=-19.3246 EndY=-64.5 EndZ=0
    g5: LineSegment StartX=-19.3246 StartY=-64.5 StartZ=0 EndX=-20.9123 EndY=-61.75 EndZ=0
    g6: Circle [constr] CenterX=-22.5 CenterY=-64.5 CenterZ=0 NormalX=0 NormalY=0 NormalZ=1 AngleXU=0 Radius=3.17543
    g7: LineSegment StartX=20.9123 StartY=-61.75 StartZ=0 EndX=19.3246 EndY=-64.5 EndZ=0
    g8: LineSegment StartX=19.3246 StartY=-64.5 StartZ=0 EndX=20.9123 EndY=-67.25 EndZ=0
    g9: LineSegment StartX=20.9123 StartY=-67.25 StartZ=0 EndX=24.0877 EndY=-67.25 EndZ=0
    g10: LineSegment StartX=24.0877 StartY=-67.25 StartZ=0 EndX=25.6754 EndY=-64.5 EndZ=0
    g11: LineSegment StartX=25.6754 StartY=-64.5 StartZ=0 EndX=24.0877 EndY=-61.75 EndZ=0
    g12: LineSegment StartX=24.0877 StartY=-61.75 StartZ=0 EndX=20.9123 EndY=-61.75 EndZ=0
    g13: Circle [constr] CenterX=22.5 CenterY=-64.5 CenterZ=0 NormalX=0 NormalY=0 NormalZ=1 AngleXU=0 Radius=3.17543
  constraints (32):
    c: Coincident(g0,g1)
    c: Coincident(g1,g2)
    c: Coincident(g2,g3)
    c: Coincident(g3,g4)
    c: Coincident(g4,g5)
    c: Coincident(g5,g0)
    c: Equal(g0, g1-g5) x5
    c: PointOnObject(g0,g6)
    c: PointOnObject(g1,g6)
    c: PointOnObject(g2,g6)
    c: PointOnObject(g3,g6)
    c: PointOnObject(g4,g6)
    c: PointOnObject(g5,g6)
    c: Coincident(g6,g-4)
    c: Coincident(g7,g8)
    c: Coincident(g8,g9)
    c: Coincident(g9,g10)
    c: Coincident(g10,g11)
    c: Coincident(g11,g12)
    c: Coincident(g12,g7)
    c: Equal(g7, g8-g12) x5
    c: PointOnObject(g7,g13)
    c: PointOnObject(g8,g13)
    c: PointOnObject(g9,g13)
    c: PointOnObject(g10,g13)
    c: PointOnObject(g11,g13)
    c: PointOnObject(g12,g13)
    c: Coincident(g13,g-3)
    c: Horizontal(g12)
    c: Horizontal(g0)
    c: Equal(g6,g13)
    c: DistanceY(g8,g7) = 5.5
FEATURE [PartDesign::Pocket] Pocket054
  BaseFeature = -> Pocket053
  Direction = (0.707107,0.707107,0)
  Length = 4
  Length2 = 5
  Profile = -> Sketch091
  ReferenceAxis = -> Sketch091 [N_Axis]
  Suppressed = false
  Type = 0
FEATURE [PartDesign::Body] Body022  label="plate"
  AllowCompound = false
  Group = -> [Binder004,Sketch089,Pad028,Sketch090,Pocket053,Sketch091,Pocket054]
  Origin = -> Origin039
  Tip = -> Pocket054
FEATURE [Sketcher::SketchObject] Sketch092
  ArcFitTolerance = 1e-06
  AttachmentSupport = -> [XY_Plane040]
  FullyConstrained = true
  MakeInternals = false
  MapMode = 5
  sketch-geometry (9):
    g0: Circle CenterX=0 CenterY=0 CenterZ=0 NormalX=0 NormalY=0 NormalZ=1 AngleXU=0 Radius=5
    g1: LineSegment [constr] StartX=-6.125 StartY=7.125 StartZ=0 EndX=-6.125 EndY=-7.125 EndZ=0
    g2: LineSegment [constr] StartX=-6.125 StartY=-7.125 StartZ=0 EndX=6.125 EndY=-7.125 EndZ=0
    g3: LineSegment [constr] StartX=6.125 StartY=-7.125 StartZ=0 EndX=6.125 EndY=7.125 EndZ=0
    g4: LineSegment [constr] StartX=6.125 StartY=7.125 StartZ=0 EndX=-6.125 EndY=7.125 EndZ=0
    g5: LineSegment StartX=-9.125 StartY=17.5 StartZ=0 EndX=-9.125 EndY=-17.5 EndZ=0
    g6: LineSegment StartX=7.625 StartY=-8.625 StartZ=0 EndX=7.625 EndY=8.625 EndZ=0
    g7: LineSegment StartX=7.625 StartY=8.625 StartZ=0 EndX=-9.125 EndY=17.5 EndZ=0
    g8: LineSegment StartX=-9.125 StartY=-17.5 StartZ=0 EndX=7.625 EndY=-8.625 EndZ=0
  constraints (23):
    c: Coincident(g0,g-1)
    c: Diameter(g0) = 10
    c: Coincident(g1,g2)
    c: Coincident(g2,g3)
    c: Coincident(g3,g4)
    c: Coincident(g4,g1)
    c: Vertical(g1)
    c: Vertical(g3)
    c: Horizontal(g2)
    c: Horizontal(g4)
    c: Symmetric(g3,g1,g0)
    c: DistanceX(g4,g4) = 12.25
    c: DistanceY(g3,g3) = 14.25
    c: DistanceX(g3,g6) = 1.5
    c: DistanceY(g3,g6) = 1.5
    c: Symmetric(g6,g6,g-1)
    c: Coincident(g7,g6)
    c: Coincident(g5,g7)
    c: Symmetric(g5,g5,g-1)
    c: Coincident(g8,g5)
    c: Coincident(g8,g6)
    c: DistanceY(g5,g5) = 35
    c: DistanceX(g5,g1) = 3
FEATURE [PartDesign::Pad] Pad029
  Direction = (0,0,1)
  Length = 15
  Length2 = 10
  Profile = -> Sketch092
  ReferenceAxis = -> Sketch092 [N_Axis]
  Reversed = true
  Suppressed = false
  Type = 0
FEATURE [Sketcher::SketchObject] Sketch093
  ArcFitTolerance = 1e-06
  AttachmentSupport = -> [Pad029]
  ExternalGeometry = -> [Pad029]
  FullyConstrained = true
  MakeInternals = false
  MapMode = 5
  Placement = pos=(7.625,4e-16,0) rot=(0.57735,0.57735,0.57735;2.0944rad)
  sketch-geometry (4):
    g0: LineSegment StartX=-7.25 StartY=0 StartZ=0 EndX=-5.25 EndY=-13 EndZ=0
    g1: LineSegment StartX=-5.25 StartY=-13 StartZ=0 EndX=5.25 EndY=-13 EndZ=0
    g2: LineSegment StartX=5.25 StartY=-13 StartZ=0 EndX=7.25 EndY=0 EndZ=0
    g3: LineSegment StartX=7.25 StartY=0 StartZ=0 EndX=-7.25 EndY=0 EndZ=0
  constraints (10):
    c: PointOnObject(g0,g-5)
    c: Coincident(g0,g1)
    c: Coincident(g1,g2)
    c: Coincident(g2,g3)
    c: Coincident(g3,g0)
    c: Symmetric(g2,g0,g-2)
    c: DistanceY(g-4,g1) = 2
    c: DistanceX(g1,g1) = 10.5
    c: Symmetric(g1,g0,g-2)
    c: DistanceX(g3,g3) = 14.5
FEATURE [PartDesign::Pocket] Pocket055
  BaseFeature = -> Pad029
  Direction = (-1,0,0)
  Length = 14
  Length2 = 5
  Profile = -> Sketch093
  ReferenceAxis = -> Sketch093 [N_Axis]
  Suppressed = false
  Type = 0
FEATURE [Sketcher::SketchObject] Sketch094
  ArcFitTolerance = 1e-06
  AttachmentSupport = -> [Pocket055]
  ExternalGeometry = -> [Pocket055]
  FullyConstrained = false
  MakeInternals = false
  MapMode = 5
  Placement = pos=(7.625,4e-16,0) rot=(0.57735,0.57735,0.57735;2.0944rad)
  sketch-geometry (5):
    g0: Circle CenterX=-13.0156 CenterY=-7.5 CenterZ=0 NormalX=0 NormalY=0 NormalZ=1 AngleXU=0 Radius=1.65
    g1: Circle CenterX=13.0156 CenterY=-7.5 CenterZ=0 NormalX=0 NormalY=0 NormalZ=1 AngleXU=0 Radius=1.65
    g2: LineSegment [constr] StartX=-7.25 StartY=0 StartZ=0 EndX=-7.25 EndY=-15 EndZ=0
    g3: GeomPoint [constr] X=-7.25 Y=-7.5 Z=0
    g4: LineSegment [constr] StartX=-13.0156 StartY=-7.5 StartZ=0 EndX=13.0156 EndY=-7.5 EndZ=0
  constraints (10):
    c: Coincident(g2,g-4)
    c: PointOnObject(g2,g-3)
    c: Vertical(g2)
    c: Symmetric(g2,g2,g3)
    c: Coincident(g4,g0)
    c: Coincident(g4,g1)
    c: PointOnObject(g3,g4)
    c: Equal(g1,g0)
    c: Symmetric(g1,g0,g-2)
    c: Diameter(g0) = 3.3
FEATURE [PartDesign::Pocket] Pocket056
  BaseFeature = -> Pocket055
  Direction = (-1,0,0)
  Length = 5
  Length2 = 5
  Profile = -> Sketch094
  ReferenceAxis = -> Sketch094 [N_Axis]
  Suppressed = false
  Type = 1
FEATURE [Sketcher::SketchObject] Sketch095
  ArcFitTolerance = 1e-06
  AttachmentSupport = -> [Pocket056]
  ExternalGeometry = -> [Pocket056]
  FullyConstrained = false
  MakeInternals = false
  MapMode = 5
  Placement = pos=(7.625,4e-16,0) rot=(0.57735,0.57735,0.57735;2.0944rad)
  sketch-geometry (8):
    g0: ArcOfCircle CenterX=-13.0156 CenterY=-7.5 CenterZ=0 NormalX=0 NormalY=0 NormalZ=1 AngleXU=0 Radius=3.75 StartAngle=4.71174 EndAngle=7.85463
    g1: ArcOfCircle CenterX=13.0156 CenterY=-7.5 CenterZ=0 NormalX=0 NormalY=0 NormalZ=1 AngleXU=0 Radius=3.75 StartAngle=1.49671 EndAngle=4.78648
    g2: LineSegment StartX=-13.018 StartY=-3.75 StartZ=0 EndX=-20.6416 EndY=-3.75 EndZ=0
    g3: LineSegment StartX=-20.6416 StartY=-3.75 StartZ=0 EndX=-20.6416 EndY=-11.25 EndZ=0
    g4: LineSegment StartX=-20.6416 StartY=-11.25 StartZ=0 EndX=-13.018 EndY=-11.25 EndZ=0
    g5: LineSegment StartX=13.2932 StartY=-11.2397 StartZ=0 EndX=24.2573 EndY=-11.2397 EndZ=0
    g6: LineSegment StartX=24.2573 StartY=-11.2397 StartZ=0 EndX=24.2573 EndY=-3.76029 EndZ=0
    g7: LineSegment StartX=24.2573 StartY=-3.76029 StartZ=0 EndX=13.2932 EndY=-3.76029 EndZ=0
  constraints (16):
    c: Coincident(g0,g-4)
    c: Coincident(g1,g-3)
    c: Coincident(g2,g3)
    c: Coincident(g3,g4)
    c: Horizontal(g2)
    c: Horizontal(g4)
    c: Vertical(g3)
    c: Coincident(g2,g0)
    c: Coincident(g5,g6)
    c: Coincident(g6,g7)
    c: Vertical(g6)
    c: Horizontal(g5)
    c: Horizontal(g7)
    c: Coincident(g0,g4)
    c: Equal(g0,g1)
    c: Radius(g1) = 3.75
FEATURE [PartDesign::Pocket] Pocket057
  BaseFeature = -> Pocket056
  Direction = (-1,0,0)
  Length = 0
  Length2 = 5
  Profile = -> Sketch095
  ReferenceAxis = -> Sketch095 [N_Axis]
  Suppressed = false
  Type = 3
  UpToFace = -> Pocket056 [Face10]
FEATURE [PartDesign::Chamfer] Chamfer004
  Angle = 45
  Base = -> Pocket057 [Edge30,Edge28]
  BaseFeature = -> Pocket057
  ChamferType = 1
  FlipDirection = false
  Size = 1
  Size2 = 1.3
  SupportTransform = false
  Suppressed = false
  UseAllEdges = false
FEATURE [PartDesign::Body] Body023  label="power_mount_main"
  AllowCompound = false
  Group = -> [Sketch092,Pad029,Sketch093,Pocket055,Sketch094,Pocket056,Sketch095,Pocket057,Chamfer004]
  Origin = -> Origin040
  Placement = pos=(0,0,-10) rot=(0,0,1;0.785398rad)
  Tip = -> Chamfer004
FEATURE [PartDesign::SubShapeBinder] Binder005
  BindCopyOnChange = 0
  BindMode = 0
  ClaimChildren = false
  Context = -> Part014 [Body024.Binder005.]
  Fuse = false
  MakeFace = true
  OffsetFill = false
  OffsetIntersection = false
  OffsetJoinType = 0
  OffsetOpenResult = false
  PartialLoad = false
  Relative = true
  Support = -> [Body022]
  _Version = 2
FEATURE [PartDesign::SubShapeBinder] Binder006
  BindCopyOnChange = 0
  BindMode = 0
  ClaimChildren = false
  Context = -> Part014 [Body024.Binder006.]
  Fuse = false
  MakeFace = true
  OffsetFill = false
  OffsetIntersection = false
  OffsetJoinType = 0
  OffsetOpenResult = false
  PartialLoad = false
  Relative = true
  Support = -> [Body023]
  _Version = 2
FEATURE [Sketcher::SketchObject] Sketch096
  ArcFitTolerance = 1e-06
  AttachmentSupport = -> [Binder005]
  ExternalGeometry = -> [Binder005,Binder006]
  FullyConstrained = false
  MakeInternals = false
  MapMode = 5
  Placement = pos=(-35.9619,1.6e-14,-7.2e-15) rot=(0.57735,0.57735,0.57735;2.0944rad)
  sketch-geometry (11):
    g0: ArcOfCircle CenterX=30 CenterY=4 CenterZ=0 NormalX=0 NormalY=0 NormalZ=1 AngleXU=0 Radius=4 StartAngle=5.57995 EndAngle=8.75618
    g1: LineSegment StartX=33.051 StartY=1.41323 StartZ=0 EndX=19.7083 EndY=-14.324 EndZ=0
    g2: LineSegment StartX=26.8612 StartY=6.47954 StartZ=0 EndX=9.8768 EndY=-15.0205 EndZ=0
    g3: ArcOfCircle CenterX=22.5 CenterY=-64.5 CenterZ=0 NormalX=0 NormalY=0 NormalZ=1 AngleXU=0 Radius=4 StartAngle=3.34071 EndAngle=6.48398
    g4: LineSegment StartX=17.8461 StartY=-21.5803 StartZ=0 EndX=26.4196 EndY=-63.7022 EndZ=0
    g5: LineSegment StartX=9.09461 StartY=-18.2912 StartZ=0 EndX=18.579 EndY=-65.2912 EndZ=0
    g6: Circle [constr] CenterX=13.0156 CenterY=-17.5 CenterZ=0 NormalX=0 NormalY=0 NormalZ=1 AngleXU=0 Radius=4
    g7: ArcOfCircle CenterX=13.0156 CenterY=-17.5 CenterZ=0 NormalX=0 NormalY=0 NormalZ=1 AngleXU=0 Radius=4 StartAngle=2.473 EndAngle=3.34071
    g8: ArcOfCircle CenterX=26.2495 CenterY=-19.8698 CenterZ=0 NormalX=0 NormalY=0 NormalZ=1 AngleXU=0 Radius=8.57571 StartAngle=2.43835 EndAngle=3.34239
    g9: GeomPoint [constr] X=17.0156 Y=-17.5 Z=0
    g10: GeomPoint X=17.6738 Y=-19.8698 Z=0
  constraints (24):
    c: Tangent(g0,g1) = 1.5708
    c: Tangent(g0,g2) = -1.5708
    c: Coincident(g0,g-3)
    c: Tangent(g3,g4) = 1.5708
    c: Tangent(g3,g5) = -1.5708
    c: Coincident(g3,g-4)
    c: PointOnObject(g2,g6)
    c: PointOnObject(g9,g6)
    c: Coincident(g7,g6)
    c: Coincident(g7,g2)
    c: Coincident(g7,g5)
    c: PointOnObject(g9,g1)
    c: PointOnObject(g9,g4)
    c: Tangent(g1,g8) = -1.5708
    c: Tangent(g4,g8) = -1.5708
    c: Radius(g3) = 4
    c: Equal(g3,g0)
    c: Diameter(g6) = 8
    c: Horizontal(g9,g6)
    c: PointOnObject(g10,g8)
    c: Horizontal(g10,g8)
    c: Coincident(g6,g-5)
    c: Angle(g7,g2,g2) = 0
    c: Angle(g5,g7,g5) = 0
FEATURE [PartDesign::Pad] Pad030
  Direction = (1,0,0)
  Length = 10
  Length2 = 10
  Profile = -> Sketch096
  ReferenceAxis = -> Sketch096 [N_Axis]
  Suppressed = false
  Type = 3
  UpToFace = -> Binder006 [Face3]
FEATURE [Sketcher::SketchObject] Sketch097
  ArcFitTolerance = 1e-06
  AttachmentSupport = -> [XZ_Plane041]
  ExternalGeometry = -> [Pad030,Binder005]
  FullyConstrained = false
  MakeInternals = false
  MapMode = 5
  Placement = pos=(0,0,0) rot=(1,0,0;1.5708rad)
  sketch-geometry (10):
    g0: LineSegment [constr] StartX=-35.9619 StartY=-0.690599 StartZ=0 EndX=-35.9619 EndY=-60.8094 EndZ=0
    g1: LineSegment [constr] StartX=-35.9619 StartY=-60.8094 StartZ=0 EndX=-13.192 EndY=-60.8094 EndZ=0
    g2: LineSegment [constr] StartX=-13.192 StartY=-60.8094 StartZ=0 EndX=-13.192 EndY=-0.690599 EndZ=0
    g3: LineSegment [constr] StartX=-13.192 StartY=-0.690599 StartZ=0 EndX=-35.9619 EndY=-0.690599 EndZ=0
    g4: LineSegment StartX=-35.9619 StartY=-61.8094 StartZ=0 EndX=-13.192 EndY=-61.8094 EndZ=0
    g5: LineSegment StartX=-13.192 StartY=-61.8094 StartZ=0 EndX=-13.192 EndY=-45 EndZ=0
    g6: LineSegment StartX=-13.192 StartY=1.3094 StartZ=0 EndX=-35.9619 EndY=1.3094 EndZ=0
    g7: LineSegment StartX=-35.9619 StartY=1.3094 StartZ=0 EndX=-35.9619 EndY=-61.8094 EndZ=0
    g8: LineSegment StartX=-13.192 StartY=1.3094 StartZ=0 EndX=-13.192 EndY=-30 EndZ=0
    g9: LineSegment StartX=-13.192 StartY=-30 StartZ=0 EndX=-13.192 EndY=-45 EndZ=0
  constraints (29):
    c: Coincident(g0,g1)
    c: Coincident(g1,g2)
    c: Coincident(g2,g3)
    c: Coincident(g3,g0)
    c: Vertical(g0)
    c: Vertical(g2)
    c: Horizontal(g1)
    c: Horizontal(g3)
    c: Horizontal(g0,g-7)
    c: Horizontal(g0,g-6)
    c: Vertical(g-5,g0)
    c: Horizontal(g4)
    c: Coincident(g5,g4)
    c: Vertical(g4,g6)
    c: Horizontal(g6)
    c: Coincident(g7,g6)
    c: Coincident(g7,g4)
    c: Vertical(g7)
    c: Vertical(g-4,g4)
    c: Coincident(g8,g6)
    c: Coincident(g9,g8)
    c: Vertical(g9)
    c: Coincident(g5,g9)
    c: Horizontal(g8,g-3)
    c: Horizontal(g5,g-3)
    c: DistanceY(g0,g6) = 2
    c: DistanceY(g4,g0) = 1
    c: PointOnObject(g8,g2)
    c: Vertical(g6,g2)
FEATURE [PartDesign::Pocket] Pocket058
  BaseFeature = -> Pad030
  Direction = (0,1,-2e-16)
  Length = 5
  Length2 = 5
  Profile = -> Sketch097
  ReferenceAxis = -> Sketch097 [N_Axis]
  Suppressed = false
  Type = 1
FEATURE [Sketcher::SketchObject] Sketch099
  ArcFitTolerance = 1e-06
  ExternalGeometry = -> [Binder005,Binder006]
  FullyConstrained = true
  MakeInternals = false
  MapMode = 5
  Placement = pos=(-10.125,0,0) rot=(0.57735,-0.57735,-0.57735;2.0944rad)
  sketch-geometry (3):
    g0: Circle CenterX=-30 CenterY=4 CenterZ=0 NormalX=0 NormalY=0 NormalZ=1 AngleXU=0 Radius=1.65
    g1: Circle CenterX=-22.5 CenterY=-64.5 CenterZ=0 NormalX=0 NormalY=0 NormalZ=1 AngleXU=0 Radius=1.65
    g2: Circle CenterX=-13.0156 CenterY=-17.5 CenterZ=0 NormalX=0 NormalY=0 NormalZ=1 AngleXU=0 Radius=1.65
  constraints (6):
    c: Coincident(g0,g-4)
    c: Equal(g0,g-4)
    c: Coincident(g1,g-3)
    c: Equal(g1,g-3)
    c: Coincident(g2,g-5)
    c: Equal(g2,g-5)
FEATURE [PartDesign::Pocket] Pocket060
  BaseFeature = -> Pocket058
  Direction = (1,0,0)
  Length = 5
  Length2 = 5
  Midplane = true
  Profile = -> Sketch099
  ReferenceAxis = -> Sketch099 [N_Axis]
  Suppressed = false
  Type = 1
FEATURE [Sketcher::SketchObject] Sketch100
  ArcFitTolerance = 1e-06
  AttachmentSupport = -> [Pocket060]
  ExternalGeometry = -> [Pocket060]
  FullyConstrained = false
  MakeInternals = false
  MapMode = 5
  Placement = pos=(-9.125,0,0) rot=(0.57735,0.57735,0.57735;2.0944rad)
  sketch-geometry (2):
    g0: Circle CenterX=30 CenterY=4 CenterZ=0 NormalX=0 NormalY=0 NormalZ=1 AngleXU=0 Radius=3
    g1: Circle CenterX=22.5 CenterY=-64.5 CenterZ=0 NormalX=0 NormalY=0 NormalZ=1 AngleXU=0 Radius=3
  constraints (3):
    c: Coincident(g1,g-3)
    c: Equal(g1,g0)
    c: Diameter(g1) = 6
FEATURE [PartDesign::Pocket] Pocket061
  BaseFeature = -> Pocket060
  Direction = (-1,0,0)
  Length = 24
  Length2 = 5
  Profile = -> Sketch100
  ReferenceAxis = -> Sketch100 [N_Axis]
  Suppressed = false
  Type = 0
FEATURE [PartDesign::Chamfer] Chamfer005
  Angle = 45
  Base = -> Pocket061 [Edge14,Edge12,Edge59,Edge61]
  BaseFeature = -> Pocket061
  ChamferType = 0
  FlipDirection = false
  Size = 1.5
  Size2 = 1
  SupportTransform = false
  Suppressed = false
  UseAllEdges = false
FEATURE [PartDesign::Fillet] Fillet010
  Base = -> Chamfer005 [Edge28,Edge38,Edge62,Edge44,Edge47,Edge59,Edge55,Edge63]
  BaseFeature = -> Chamfer005
  Radius = 0.5
  SupportTransform = false
  Suppressed = false
  UseAllEdges = false
FEATURE [Sketcher::SketchObject] Sketch101
  ArcFitTolerance = 1e-06
  AttachmentSupport = -> [Fillet010]
  ExternalGeometry = -> [Fillet010]
  FullyConstrained = true
  MakeInternals = false
  MapMode = 5
  Placement = pos=(-13.192,0,8e-16) rot=(0.57735,-0.57735,-0.57735;2.0944rad)
  sketch-geometry (7):
    g0: LineSegment StartX=-11.4279 StartY=-14.75 StartZ=0 EndX=-14.6033 EndY=-14.75 EndZ=0
    g1: LineSegment StartX=-14.6033 StartY=-14.75 StartZ=0 EndX=-16.191 EndY=-17.5 EndZ=0
    g2: LineSegment StartX=-16.191 StartY=-17.5 StartZ=0 EndX=-14.6033 EndY=-20.25 EndZ=0
    g3: LineSegment StartX=-14.6033 StartY=-20.25 StartZ=0 EndX=-11.4279 EndY=-20.25 EndZ=0
    g4: LineSegment StartX=-11.4279 StartY=-20.25 StartZ=0 EndX=-9.84014 EndY=-17.5 EndZ=0
    g5: LineSegment StartX=-9.84014 StartY=-17.5 StartZ=0 EndX=-11.4279 EndY=-14.75 EndZ=0
    g6: Circle [constr] CenterX=-13.0156 CenterY=-17.5 CenterZ=0 NormalX=0 NormalY=0 NormalZ=1 AngleXU=0 Radius=3.17543
  constraints (16):
    c: Coincident(g0,g1)
    c: Coincident(g1,g2)
    c: Coincident(g2,g3)
    c: Coincident(g3,g4)
    c: Coincident(g4,g5)
    c: Coincident(g5,g0)
    c: Equal(g0, g1-g5) x5
    c: PointOnObject(g0,g6)
    c: PointOnObject(g1,g6)
    c: PointOnObject(g2,g6)
    c: PointOnObject(g3,g6)
    c: PointOnObject(g4,g6)
    c: PointOnObject(g5,g6)
    c: Coincident(g6,g-3)
    c: Horizontal(g0)
    c: Distance(g0,g1) = 5.5
FEATURE [PartDesign::Pocket] Pocket062
  BaseFeature = -> Fillet010
  Direction = (1,0,0)
  Length = 2
  Length2 = 5
  Profile = -> Sketch101
  ReferenceAxis = -> Sketch101 [N_Axis]
  Suppressed = false
  Type = 0
FEATURE [PartDesign::Body] Body024  label="power_mount_bracket"
  AllowCompound = false
  Group = -> [Binder005,Binder006,Sketch096,Pad030,Sketch097,Pocket058,Sketch099,Pocket060,Sketch100,Pocket061,Chamfer005,Fillet010,Sketch101,Pocket062]
  Origin = -> Origin041
  Placement = pos=(0,0,0) rot=(0,0,1;0.785398rad)
  Tip = -> Pocket062
COMPONENT P11 — recipe-attached ("studs", modeled in this document).
Construction recipe (the document's own serialized feature program — sketch geometry with constraints, then the solid features built on it; lengths are millimeters unless a unit is written):

FEATURE [PartDesign::SubShapeBinder] Binder007
  BindCopyOnChange = 0
  BindMode = 0
  ClaimChildren = false
  Context = -> Part015 [Body025.Binder007.]
  Fuse = false
  MakeFace = true
  OffsetFill = false
  OffsetIntersection = false
  OffsetJoinType = 0
  OffsetOpenResult = false
  PartialLoad = false
  Relative = true
  Support = -> [Part001[Body001.Pocket003.Face4]]
  _Version = 2
FEATURE [Sketcher::SketchObject] Sketch102
  ArcFitTolerance = 1e-06
  AttachmentSupport = -> [Binder007]
  ExternalGeometry = -> [Binder007]
  FullyConstrained = true
  MakeInternals = false
  MapMode = 5
  Placement = pos=(-2.8168e-05,-1.91593e-06,-20) rot=(1,0,-1e-06;3.14159rad)
  sketch-geometry (5):
    g0: Circle CenterX=2.8168e-05 CenterY=93.3381 CenterZ=0 NormalX=0 NormalY=0 NormalZ=1 AngleXU=0 Radius=2.15
    g1: LineSegment StartX=-4.12497 StartY=97.6952 StartZ=0 EndX=4.12503 EndY=97.6952 EndZ=0
    g2: ArcOfCircle CenterX=2.8168e-05 CenterY=93.3381 CenterZ=0 NormalX=0 NormalY=0 NormalZ=1 AngleXU=0 Radius=6 StartAngle=2.32884 EndAngle=7.09594
    g3: Circle [constr] CenterX=2.8168e-05 CenterY=93.3381 CenterZ=0 NormalX=0 NormalY=0 NormalZ=1 AngleXU=0 Radius=4
    g4: GeomPoint [constr] X=0 Y=89.3381 Z=0
  constraints (13):
    c: Coincident(g0,g-3)
    c: Diameter(g0) = 4.3
    c: Horizontal(g1)
    c: Coincident(g2,g0)
    c: Coincident(g2,g1)
    c: Coincident(g2,g1)
    c: Radius(g2) = 6
    c: DistanceX(g1,g1) = 8.25
    c: Coincident(g3,g0)
    c: Diameter(g3) = 8
    c: PointOnObject(g4,g3)
    c: PointOnObject(g4,g-2)
    c: DistanceY(g4,g1) = 8.35711
FEATURE [PartDesign::Pad] Pad031
  Direction = (-1.4084e-06,-9.57964e-08,-1)
  Length = 70
  Length2 = 10
  Profile = -> Sketch102
  ReferenceAxis = -> Sketch102 [N_Axis]
  Suppressed = false
  Type = 0
FEATURE [Sketcher::SketchObject] Sketch103
  ArcFitTolerance = 1e-06
  AttachmentSupport = -> [Pad031]
  ExternalGeometry = -> [Pad031]
  FullyConstrained = true
  MakeInternals = false
  MapMode = 5
  Placement = pos=(0,-97.6952,9.35885e-06) rot=(1,0,0;1.5708rad)
  sketch-geometry (4):
    g0: LineSegment StartX=-4.12501 StartY=-25 StartZ=0 EndX=-4.12501 EndY=-81 EndZ=0
    g1: LineSegment StartX=-4.12501 StartY=-81 StartZ=0 EndX=4.12491 EndY=-81 EndZ=0
    g2: LineSegment StartX=4.12491 StartY=-81 StartZ=0 EndX=4.12491 EndY=-25 EndZ=0
    g3: LineSegment StartX=4.12491 StartY=-25 StartZ=0 EndX=-4.12501 EndY=-25 EndZ=0
  constraints (12):
    c: Coincident(g0,g1)
    c: Coincident(g1,g2)
    c: Coincident(g2,g3)
    c: Coincident(g3,g0)
    c: Vertical(g0)
    c: Vertical(g2)
    c: Horizontal(g1)
    c: Horizontal(g3)
    c: PointOnObject(g0,g-3)
    c: PointOnObject(g1,g-4)
    c: DistanceY(g2,g-4) = 5
    c: DistanceY(g-4,g1) = 9
FEATURE [PartDesign::Pocket] Pocket063
  BaseFeature = -> Pad031
  Direction = (0,1,-9.57964e-08)
  Length = 8
  Length2 = 5
  Profile = -> Sketch103
  ReferenceAxis = -> Sketch103 [N_Axis]
  Suppressed = false
  Type = 0
FEATURE [Sketcher::SketchObject] Sketch104
  ArcFitTolerance = 1e-06
  AttachmentSupport = -> [Pocket063]
  ExternalGeometry = -> [Pocket063]
  FullyConstrained = true
  MakeInternals = false
  MapMode = 5
  Placement = pos=(0,-7.75951e-06,-81) rot=(-1.03323,0,0;0rad)
  sketch-geometry (7):
    g0: LineSegment StartX=-2.02073 StartY=-89.8381 StartZ=0 EndX=-4.04145 EndY=-93.3381 EndZ=0
    g1: LineSegment StartX=-4.04145 StartY=-93.3381 StartZ=0 EndX=-2.02073 EndY=-96.8381 EndZ=0
    g2: LineSegment StartX=-2.02073 StartY=-96.8381 StartZ=0 EndX=2.02073 EndY=-96.8381 EndZ=0
    g3: LineSegment StartX=2.02073 StartY=-96.8381 StartZ=0 EndX=4.04145 EndY=-93.3381 EndZ=0
    g4: LineSegment StartX=4.04145 StartY=-93.3381 StartZ=0 EndX=2.02073 EndY=-89.8381 EndZ=0
    g5: LineSegment StartX=2.02073 StartY=-89.8381 StartZ=0 EndX=-2.02073 EndY=-89.8381 EndZ=0
    g6: Circle [constr] CenterX=-4.50824e-11 CenterY=-93.3381 CenterZ=0 NormalX=0 NormalY=0 NormalZ=1 AngleXU=0 Radius=4.04145
  constraints (16):
    c: Coincident(g0,g1)
    c: Coincident(g1,g2)
    c: Coincident(g2,g3)
    c: Coincident(g3,g4)
    c: Coincident(g4,g5)
    c: Coincident(g5,g0)
    c: Equal(g0, g1-g5) x5
    c: PointOnObject(g0,g6)
    c: PointOnObject(g1,g6)
    c: PointOnObject(g2,g6)
    c: PointOnObject(g3,g6)
    c: PointOnObject(g4,g6)
    c: PointOnObject(g5,g6)
    c: Coincident(g6,g-3)
    c: Horizontal(g5)
    c: Distance(g4,g0) = 7
FEATURE [PartDesign::Pocket] Pocket064
  BaseFeature = -> Pocket063
  Direction = (0,-9.57964e-08,-1)
  Length = 4
  Length2 = 5
  Profile = -> Sketch104
  ReferenceAxis = -> Sketch104 [N_Axis]
  Suppressed = false
  Type = 0
FEATURE [PartDesign::Body] Body025
  AllowCompound = false
  Group = -> [Binder007,Sketch102,Pad031,Sketch103,Pocket063,Sketch104,Pocket064]
  Origin = -> Origin043
  Tip = -> Pocket064
COMPONENT P12 — recipe-attached ("_inner", modeled in this document).
Construction recipe (the document's own serialized feature program — sketch geometry with constraints, then the solid features built on it; lengths are millimeters unless a unit is written):

FEATURE [PartDesign::SubShapeBinder] Binder008
  BindCopyOnChange = 0
  BindMode = 0
  ClaimChildren = false
  Context = -> Part016 [Body026.Binder008.]
  Fuse = false
  MakeFace = true
  OffsetFill = false
  OffsetIntersection = false
  OffsetJoinType = 0
  OffsetOpenResult = false
  PartialLoad = false
  Placement = pos=(0,0,-9) rot=(0,0,1;0rad)
  Relative = true
  Support = -> [Part005[Body007.Chamfer002.Face62]]
  _Version = 2
FEATURE [Sketcher::SketchObject] Sketch105
  ArcFitTolerance = 1e-06
  AttachmentSupport = -> [Binder008]
  ExternalGeometry = -> [Binder008]
  FullyConstrained = false
  MakeInternals = false
  MapMode = 5
  Placement = pos=(0,0,0) rot=(1,0,0;3.14159rad)
  sketch-geometry (13):
    g0: ArcOfCircle CenterX=56 CenterY=-56 CenterZ=0 NormalX=0 NormalY=0 NormalZ=1 AngleXU=0 Radius=5 StartAngle=4.71239 EndAngle=6.28319
    g1: ArcOfCircle CenterX=-56 CenterY=-56 CenterZ=0 NormalX=0 NormalY=0 NormalZ=1 AngleXU=0 Radius=5 StartAngle=1.86718 EndAngle=4.71239
    g2: LineSegment StartX=56 StartY=-61 StartZ=0 EndX=-56 EndY=-61 EndZ=0
    g3: Circle CenterX=56 CenterY=-56 CenterZ=0 NormalX=0 NormalY=0 NormalZ=1 AngleXU=0 Radius=2.25
    g4: Circle CenterX=-56 CenterY=-56 CenterZ=0 NormalX=0 NormalY=0 NormalZ=1 AngleXU=0 Radius=2.23266
    g5: LineSegment StartX=-57.4603 StartY=-51.218 StartZ=0 EndX=-26.3893 EndY=-41.7296 EndZ=0
    g6: LineSegment StartX=61 StartY=-56 StartZ=0 EndX=61 EndY=-41 EndZ=0
    g7: LineSegment StartX=-21.5018 StartY=-41 StartZ=0 EndX=61 EndY=-41 EndZ=0
    g8: Circle CenterX=56 CenterY=-46 CenterZ=0 NormalX=0 NormalY=0 NormalZ=1 AngleXU=0 Radius=0.625
    g9: Circle CenterX=-24 CenterY=-45.6829 CenterZ=0 NormalX=0 NormalY=0 NormalZ=1 AngleXU=0 Radius=0.625
    g10: LineSegment [constr] StartX=-24 StartY=-45.6829 StartZ=0 EndX=56 EndY=-46 EndZ=0
    g11: ArcOfCircle CenterX=-21.5018 CenterY=-57.7344 CenterZ=0 NormalX=0 NormalY=0 NormalZ=1 AngleXU=0 Radius=16.7344 StartAngle=1.5708 EndAngle=1.86718
    g12: GeomPoint [constr] X=-24 Y=-41 Z=0
  constraints (28):
    c: Tangent(g0,g2) = 1.5708
    c: Tangent(g1,g2) = 1.5708
    c: Coincident(g1,g-3)
    c: Coincident(g-4,g0)
    c: Coincident(g3,g0)
    c: Coincident(g4,g1)
    c: Radius(g1) = 5
    c: Coincident(g5,g1)
    c: Coincident(g7,g6)
    c: Diameter(g8) = 1.25
    c: Equal(g8,g9)
    c: Coincident(g10,g9)
    c: Coincident(g10,g8)
    c: DistanceX(g10,g10) = 80
    c: DistanceY(g0,g8) = 10
    c: Angle(g6,g0,g0) = 0
    c: Coincident(g6,g0)
    c: Equal(g1,g0)
    c: Vertical(g8,g0)
    c: Vertical(g6)
    c: DistanceY(g8,g6) = 5
    c: Angle(g5,g1,g1) = 3.14159
    c: PointOnObject(g12,g5)
    c: PointOnObject(g12,g7)
    c: Tangent(g5,g11) = 1.5708
    c: Tangent(g7,g11) = 1.5708
    c: Horizontal(g7)
    c: Vertical(g12,g9)
FEATURE [PartDesign::Pad] Pad036
  Direction = (0,0,-1)
  Length = 15
  Length2 = 10
  Placement = pos=(0,0,-9) rot=(0,0,1;0rad)
  Profile = -> Sketch105
  ReferenceAxis = -> Sketch105 [N_Axis]
  Suppressed = false
  Type = 0
FEATURE [Sketcher::SketchObject] Sketch111
  ArcFitTolerance = 1e-06
  AttachmentSupport = -> [Pad036]
  ExternalGeometry = -> [Pad036]
  FullyConstrained = false
  MakeInternals = false
  MapMode = 5
  Placement = pos=(0,61,-9) rot=(0,0.707107,0.707107;3.14159rad)
  sketch-geometry (26):
    g0: LineSegment StartX=-48.7673 StartY=9 StartZ=0 EndX=48.7673 EndY=9 EndZ=0
    g1-g5: Circle [constr] x5 (B-spline internal-alignment scaffolding for g6; pole/knot coordinates omitted)
    g6: BSplineCurve PolesCount=5 KnotsCount=3 Degree=3 IsPeriodic=0
    g7: GeomPoint [constr] X=-48.7673 Y=9 Z=0
    g8: GeomPoint [constr] X=0 Y=-2 Z=0
    g9: GeomPoint [constr] X=48.7673 Y=9 Z=0
    g10: LineSegment StartX=61 StartY=-6 StartZ=0 EndX=61 EndY=5 EndZ=0
    g11: LineSegment StartX=61 StartY=5 StartZ=0 EndX=50.7673 EndY=5 EndZ=0
    g12: LineSegment StartX=61 StartY=-6 StartZ=0 EndX=27.625 EndY=-6 EndZ=0
    g13: LineSegment StartX=-61 StartY=-6 StartZ=0 EndX=-57.9232 EndY=-6 EndZ=0
    g14: LineSegment StartX=-61 StartY=-6 StartZ=0 EndX=-61 EndY=5 EndZ=0
    g15: LineSegment StartX=-61 StartY=5 StartZ=0 EndX=-57.9232 EndY=5 EndZ=0
    g16-g20: Circle [constr] x5 (B-spline internal-alignment scaffolding for g21; pole/knot coordinates omitted)
    g21: BSplineCurve PolesCount=5 KnotsCount=3 Degree=3 IsPeriodic=0
    g22: GeomPoint [constr] X=27.625 Y=-6 Z=0
    g23: GeomPoint [constr] X=39.6768 Y=-2.95477 Z=0
    g24: GeomPoint [constr] X=50.7673 Y=5 Z=0
    g25: LineSegment StartX=-57.9232 StartY=-6 StartZ=0 EndX=-57.9232 EndY=5 EndZ=0
  constraints (45):
    c: Horizontal(g0,g-4)
    c: Symmetric(g0,g0,g-2)
    c: DistanceX(g0,g-4) = 5
    c: Weight(g1) = 1
    c: Equal(g1, g2-g5) x4
    c: InternalAlignment(g1-g5 -> g6) x5
    c: InternalAlignment(g7,g6)
    c: InternalAlignment(g8,g6)
    c: InternalAlignment(g9,g6)
    c: Coincident(g1,g0)
    c: PointOnObject(g3,g-2)
    c: Coincident(g5,g0)
    c: Vertical(g6,g4)
    c: Symmetric(g2,g4,g-2)
    c: DistanceY(g-5,g8) = 4
    c: Horizontal(g4,g8)
    c: Coincident(g-7,g10)
    c: Vertical(g10)
    c: Coincident(g10,g11)
    c: Coincident(g10,g12)
    c: Horizontal(g12)
    c: Coincident(g-8,g13)
    c: Horizontal(g13)
    c: Coincident(g13,g14)
    c: Vertical(g14)
    c: Coincident(g14,g15)
    c: Horizontal(g15)
    c: Horizontal(g11)
    c: DistanceY(g10,g-4) = 4
    c: DistanceX(g-4,g11) = -3
    c: DistanceX(g-5,g12) = 3
    c: Weight(g16) = 1
    c: Equal(g16, g17-g20) x4
    c: InternalAlignment(g16-g20 -> g21) x5
    c: InternalAlignment(g22,g21)
    c: InternalAlignment(g23,g21)
    c: InternalAlignment(g24,g21)
    c: Coincident(g16,g12)
    c: PointOnObject(g17,g12)
    c: Coincident(g20,g11)
    c: Vertical(g19,g21)
    c: Coincident(g25,g13)
    c: Coincident(g25,g15)
    c: Horizontal(g15,g21)
    c: Vertical(g25)
FEATURE [PartDesign::Pocket] Pocket067
  BaseFeature = -> Pad036
  Direction = (0,-1,2e-16)
  Length = 5
  Length2 = 5
  Placement = pos=(0,0,-9) rot=(0,0,1;0rad)
  Profile = -> Sketch111
  ReferenceAxis = -> Sketch111 [N_Axis]
  Suppressed = false
  Type = 1
FEATURE [Sketcher::SketchObject] Sketch112
  ArcFitTolerance = 1e-06
  AttachmentSupport = -> [Pocket067]
  ExternalGeometry = -> [Pocket067]
  FullyConstrained = false
  MakeInternals = false
  MapMode = 5
  Placement = pos=(0,0,-15) rot=(1,0,0;3.14159rad)
  sketch-geometry (20):
    g0: LineSegment StartX=-48.7673 StartY=-61 StartZ=0 EndX=48.7673 EndY=-61 EndZ=0
    g1-g5: Circle [constr] x5 (B-spline internal-alignment scaffolding for g6; pole/knot coordinates omitted)
    g6: BSplineCurve PolesCount=5 KnotsCount=3 Degree=3 IsPeriodic=0
    g7: GeomPoint [constr] X=-22.3038 Y=-41 Z=0
    g8: GeomPoint [constr] X=18.1075 Y=-46.1752 Z=0
    g9: GeomPoint [constr] X=52.2839 Y=-41 Z=0
    g10-g14: Circle [constr] x5 (B-spline internal-alignment scaffolding for g15; pole/knot coordinates omitted)
    g15: BSplineCurve PolesCount=5 KnotsCount=3 Degree=3 IsPeriodic=0
    g16: GeomPoint [constr] X=-48.7673 Y=-61 Z=0
    g17: GeomPoint [constr] X=15.8447 Y=-52.7433 Z=0
    g18: GeomPoint [constr] X=48.7673 Y=-61 Z=0
    g19: LineSegment StartX=-22.3038 StartY=-41 StartZ=0 EndX=52.2839 EndY=-41 EndZ=0
  constraints (20):
    c: Coincident(g-4,g0)
    c: Coincident(g0,g-3)
    c: Weight(g1) = 1
    c: Equal(g1, g2-g5) x4
    c: InternalAlignment(g1-g5 -> g6) x5
    c: InternalAlignment(g7,g6)
    c: InternalAlignment(g8,g6)
    c: InternalAlignment(g9,g6)
    c: Weight(g10) = 1
    c: Equal(g10, g11-g14) x4
    c: InternalAlignment(g10-g14 -> g15) x5
    c: InternalAlignment(g16,g15)
    c: InternalAlignment(g17,g15)
    c: InternalAlignment(g18,g15)
    c: Coincident(g10,g0)
    c: Coincident(g15,g0)
    c: Coincident(g19,g6)
    c: Horizontal(g19)
    c: Coincident(g6,g19)
    c: Horizontal(g6,g-3)
FEATURE [PartDesign::Pocket] Pocket068
  BaseFeature = -> Pocket067
  Direction = (0,0,1)
  Length = 5
  Length2 = 5
  Placement = pos=(0,0,-9) rot=(0,0,1;0rad)
  Profile = -> Sketch112
  ReferenceAxis = -> Sketch112 [N_Axis]
  Suppressed = false
  Type = 1
FEATURE [Sketcher::SketchObject] Sketch113
  ArcFitTolerance = 1e-06
  AttachmentSupport = -> [Pocket068]
  ExternalGeometry = -> [Pocket068]
  FullyConstrained = true
  MakeInternals = false
  MapMode = 5
  Placement = pos=(61,0,-9) rot=(0.57735,0.57735,0.57735;2.0944rad)
  sketch-geometry (4):
    g0: LineSegment StartX=51.8259 StartY=-6 StartZ=0 EndX=51.8259 EndY=5 EndZ=0
    g1: LineSegment StartX=51.8259 StartY=5 StartZ=0 EndX=61 EndY=5 EndZ=0
    g2: LineSegment StartX=61 StartY=5 StartZ=0 EndX=61 EndY=-6 EndZ=0
    g3: LineSegment StartX=61 StartY=-6 StartZ=0 EndX=51.8259 EndY=-6 EndZ=0
  constraints (10):
    c: Coincident(g0,g-3)
    c: Vertical(g0)
    c: Coincident(g1,g0)
    c: Horizontal(g1)
    c: Coincident(g2,g1)
    c: Coincident(g3,g2)
    c: Coincident(g3,g0)
    c: Coincident(g2,g-3)
    c: Vertical(g2)
    c: PointOnObject(g0,g-4)
FEATURE [PartDesign::Pocket] Pocket069
  BaseFeature = -> Pocket068
  Direction = (-1,0,0)
  Length = 13
  Length2 = 5
  Placement = pos=(0,0,-9) rot=(0,0,1;0rad)
  Profile = -> Sketch113
  ReferenceAxis = -> Sketch113 [N_Axis]
  Suppressed = false
  Type = 0
FEATURE [PartDesign::Body] Body026
  AllowCompound = false
  Group = -> [Binder008,Sketch105,Pad036,Sketch111,Pocket067,Sketch112,Pocket068,Sketch113,Pocket069]
  Origin = -> Origin045
  Tip = -> Pocket069
COMPONENT P13 — recipe-attached ("new_usb_hub", modeled in this document).
Construction recipe (the document's own serialized feature program — sketch geometry with constraints, then the solid features built on it; lengths are millimeters unless a unit is written):

FEATURE [Sketcher::SketchObject] Sketch109
  ArcFitTolerance = 1e-06
  AttachmentSupport = -> [XY_Plane046]
  FullyConstrained = true
  MakeInternals = false
  MapMode = 5
  sketch-geometry (4):
    g0: LineSegment StartX=-60.5 StartY=17.5 StartZ=0 EndX=-60.5 EndY=-17.5 EndZ=0
    g1: LineSegment StartX=-60.5 StartY=-17.5 StartZ=0 EndX=60.5 EndY=-17.5 EndZ=0
    g2: LineSegment StartX=60.5 StartY=-17.5 StartZ=0 EndX=60.5 EndY=17.5 EndZ=0
    g3: LineSegment StartX=60.5 StartY=17.5 StartZ=0 EndX=-60.5 EndY=17.5 EndZ=0
  constraints (11):
    c: Coincident(g0,g1)
    c: Coincident(g1,g2)
    c: Coincident(g2,g3)
    c: Coincident(g3,g0)
    c: Vertical(g0)
    c: Vertical(g2)
    c: Horizontal(g1)
    c: Horizontal(g3)
    c: Symmetric(g2,g0,g-1)
    c: DistanceY(g2,g2) = 35
    c: DistanceX(g3,g3) = 121
FEATURE [PartDesign::Pad] Pad035
  Direction = (0,0,1)
  Length = 19
  Length2 = 10
  Profile = -> Sketch109
  ReferenceAxis = -> Sketch109 [N_Axis]
  Suppressed = false
  Type = 0
FEATURE [Sketcher::SketchObject] Sketch110
  ArcFitTolerance = 1e-06
  AttachmentSupport = -> [Pad035]
  ExternalGeometry = -> [Pad035]
  FullyConstrained = true
  MakeInternals = false
  MapMode = 5
  Placement = pos=(60.5,0,0) rot=(0.57735,0.57735,0.57735;2.0944rad)
  sketch-geometry (8):
    g0: LineSegment StartX=-17.5 StartY=0 StartZ=0 EndX=-16.75 EndY=12 EndZ=0
    g1: LineSegment StartX=-16.75 StartY=12 StartZ=0 EndX=-9.75 EndY=19 EndZ=0
    g2: LineSegment StartX=-9.75 StartY=19 StartZ=0 EndX=9.75 EndY=19 EndZ=0
    g3: LineSegment StartX=9.75 StartY=19 StartZ=0 EndX=16.75 EndY=12 EndZ=0
    g4: LineSegment StartX=16.75 StartY=12 StartZ=0 EndX=17.5 EndY=0 EndZ=0
    g5: LineSegment StartX=17.5 StartY=0 StartZ=0 EndX=17.5 EndY=20 EndZ=0
    g6: LineSegment StartX=17.5 StartY=20 StartZ=0 EndX=-17.5 EndY=20 EndZ=0
    g7: LineSegment StartX=-17.5 StartY=20 StartZ=0 EndX=-17.5 EndY=0 EndZ=0
  constraints (19):
    c: Coincident(g0,g-3)
    c: Coincident(g1,g0)
    c: Coincident(g2,g1)
    c: Coincident(g3,g2)
    c: Coincident(g4,g3)
    c: Coincident(g4,g-3)
    c: Coincident(g5,g4)
    c: Vertical(g5)
    c: Coincident(g6,g5)
    c: Coincident(g7,g6)
    c: Coincident(g7,g0)
    c: Symmetric(g5,g6,g-2)
    c: Symmetric(g2,g1,g-2)
    c: Symmetric(g3,g0,g-2)
    c: DistanceY(g4,g2) = 19
    c: DistanceY(g5,g5) = 20
    c: DistanceX(g0,g3) = 33.5
    c: DistanceX(g2,g2) = 19.5
    c: DistanceY(g4,g3) = 12
FEATURE [PartDesign::Pocket] Pocket066
  BaseFeature = -> Pad035
  Direction = (-1,0,0)
  Length = 5
  Length2 = 5
  Profile = -> Sketch110
  ReferenceAxis = -> Sketch110 [N_Axis]
  Suppressed = false
  Type = 1
FEATURE [PartDesign::Body] Body027  label="usbhub"
  AllowCompound = false
  Group = -> [Sketch109,Pad035,Sketch110,Pocket066]
  Origin = -> Origin046
  Tip = -> Pocket066
PROVENANCE & LICENSES
A FreeCAD (.FCStd) document from a public repository crawl; recipes are the document's own serialized feature recipes (and, for linked parts, companion documents' recipes).
License: mit.
